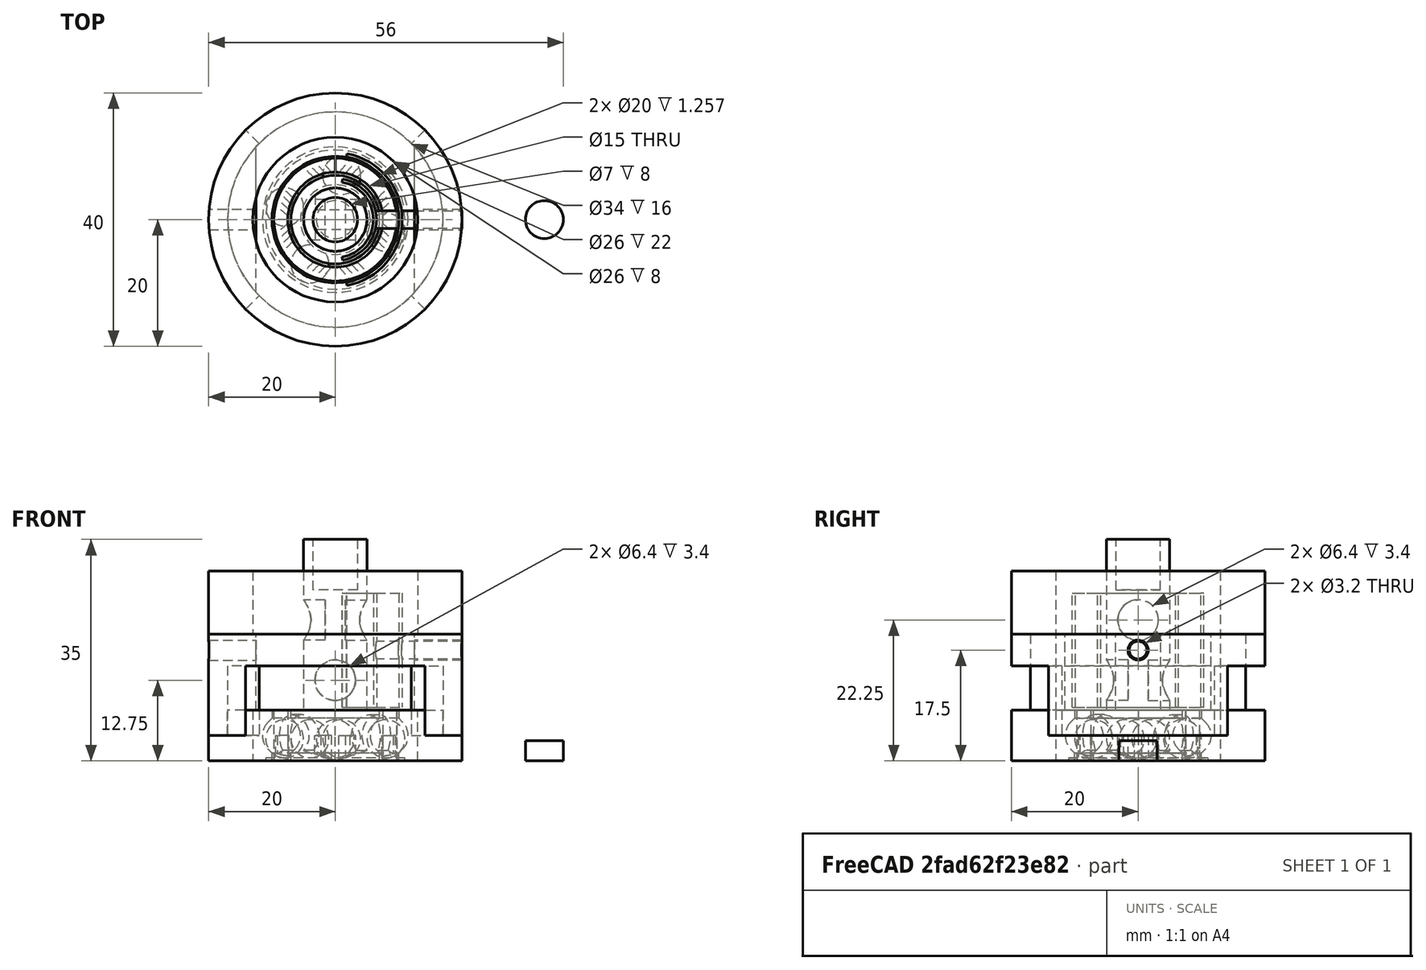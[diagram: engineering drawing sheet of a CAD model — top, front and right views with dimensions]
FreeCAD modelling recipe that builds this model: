
FCSTD DOCUMENT  (FreeCAD 1.2R20260106 (Git shallow))
Label: laser
License: MIT
LicenseURL: https://en.wikipedia.org/wiki/MIT_License
objects: Sketcher::SketchObject×27, App::FeaturePython×20, App::Link×11, PartDesign::Pocket×10, PartDesign::SubShapeBinder×10, PartDesign::Pad×9, App::Point×8, PartDesign::Body×6, Part::Sphere×6, PartDesign::Plane×5, Part::FeaturePython×4, PartDesign::Revolution×2, Part::Cylinder×2, PartDesign::Mirrored×2, Part::Compound×1, Spreadsheet::Sheet×1, Part::Extrusion×1, Part::Loft×1, Assembly::ViewGroup×1, Part::MultiFuse×1, +4 more types
note: 159 computed .brp shape members not serialized (recipe doc carries the construction recipe); baked Part::Feature solids carry a one-line shape summary decoded from their .brp

FEATURE [Sketcher::SketchObject] Sketch
  ArcFitTolerance = 1e-06
  AttachmentSupport = -> [XY_Plane]
  ExternalTypes = [0]
  FullyConstrained = true
  MakeInternals = false
  MapMode = 5
  sketch-geometry (2):
    g0: Circle CenterX=0 CenterY=0 CenterZ=0 NormalX=0 NormalY=0 NormalZ=1 AngleXU=0 Radius=5
    g1: GeomPoint X=0 Y=0 Z=0
  constraints (3):
    c: Diameter(g0) = 10
    c: Coincident(g1,g-1)
    c: Coincident(g0,g1)
FEATURE [PartDesign::Pad] Pad
  Direction = (0,0,1)
  Length = 35
  Length2 = 10
  Profile = -> Sketch
  ReferenceAxis = -> Sketch [N_Axis]
  Refine = true
  SideType = 0
  Suppressed = false
  Type = 0
  Type2 = 0
FEATURE [Sketcher::SketchObject] Sketch019
  ArcFitTolerance = 1e-06
  ExternalTypes = [0]
  FullyConstrained = true
  MakeInternals = false
  MapMode = 5
  Placement = pos=(0,0,35) rot=(0,0,1;0rad)
  sketch-geometry (1):
    g0: Circle CenterX=0 CenterY=0 CenterZ=0 NormalX=0 NormalY=0 NormalZ=1 AngleXU=0 Radius=3.5
  constraints (2):
    c: Diameter(g0) = 7
    c: Coincident(g0,g-1)
FEATURE [PartDesign::Pocket] Pocket007
  BaseFeature = -> Pad
  Direction = (0,0,-1)
  Length = 8
  Length2 = 5
  Profile = -> Sketch019
  ReferenceAxis = -> Sketch019 [N_Axis]
  Refine = true
  SideType = 0
  Suppressed = false
  Type = 0
  Type2 = 0
FEATURE [App::Link] rotor  label="rotor001"
  LinkPlacement = pos=(0,0,0) rot=(0,0,1;2.35834rad)
  LinkedObject = -> Body
  Placement = pos=(0,0,0) rot=(0,0,1;2.35834rad)
FEATURE [Sketcher::SketchObject] Sketch031
  ArcFitTolerance = 1e-06
  AttachmentSupport = -> [Pocket007]
  ExternalGeometry = -> [Pad]
  ExternalTypes = [0]
  FullyConstrained = true
  MakeInternals = false
  MapMode = 5
  Placement = pos=(0,0,35) rot=(0,0,1;0rad)
  sketch-geometry (4):
    g0: LineSegment StartX=0 StartY=0 StartZ=0 EndX=3e-16 EndY=5 EndZ=0
    g1: LineSegment StartX=0 StartY=0 StartZ=0 EndX=-5 EndY=-1e-16 EndZ=0
    g2: LineSegment StartX=0 StartY=0 StartZ=0 EndX=5 EndY=0 EndZ=0
    g3: LineSegment StartX=0 StartY=0 StartZ=0 EndX=-3.305e-13 EndY=-5 EndZ=0
  constraints (12):
    c: Coincident(g0,g-1)
    c: PointOnObject(g0,g-3)
    c: Angle(g-1,g0) = 1.5708
    c: Coincident(g1,g0)
    c: PointOnObject(g1,g-3)
    c: Angle(g1,g-1) = 3.14159
    c: Coincident(g3,g2)
    c: Coincident(g2,g0)
    c: PointOnObject(g3,g-3)
    c: PointOnObject(g2,g-3)
    c: Angle(g-1,g2) = 0
    c: Angle(g3,g-1) = 1.5708
FEATURE [PartDesign::Plane] DatumPlane  label="p2"
  AttachmentOffset = pos=(0,0,0) rot=(0,1,0;3.14159rad)
  AttachmentSupport = -> [Sketch031]
  Length = 60.9545
  MapMode = 7
  Placement = pos=(3e-16,5,35) rot=(0,0.707107,0.707107;3.14159rad)
  ResizeMode = 0
  Width = 70.9545
FEATURE [PartDesign::Plane] DatumPlane003  label="p3"
  AttachmentOffset = pos=(0,0,0) rot=(0,1,0;3.14159rad)
  AttachmentSupport = -> [Sketch031]
  Length = 60.9545
  MapMode = 7
  Placement = pos=(-5,-1e-16,35) rot=(-0.57735,0.57735,0.57735;4.18879rad)
  ResizeMode = 0
  Width = 70.9545
FEATURE [PartDesign::Plane] DatumPlane004  label="p4"
  AttachmentOffset = pos=(0,0,0) rot=(0,1,0;3.14159rad)
  AttachmentSupport = -> [Sketch031]
  Length = 60.9545
  MapMode = 7
  Placement = pos=(5,0,35) rot=(0.57735,0.57735,0.57735;2.0944rad)
  ResizeMode = 0
  Width = 70.9545
FEATURE [PartDesign::Plane] DatumPlane002  label="p1"
  AttachmentOffset = pos=(0,0,0) rot=(0,1,0;3.14159rad)
  AttachmentSupport = -> [Sketch031]
  Length = 60.9545
  MapMode = 7
  Placement = pos=(-3.305e-13,-5,35) rot=(-1,0,0;4.71239rad)
  ResizeMode = 0
  Width = 70.9545
FEATURE [Sketcher::SketchObject] Sketch034
  ArcFitTolerance = 1e-06
  AttachmentSupport = -> [XZ_Plane]
  ExternalTypes = [0]
  FullyConstrained = true
  MakeInternals = false
  MapMode = 5
  Placement = pos=(0,0,0) rot=(1,0,0;1.5708rad)
  expr: Constraints[13] = Spreadsheet.bearing_ball_radius
  expr: Constraints[38] = Spreadsheet.bearing_ball_radius + Spreadsheet.bearing_ball_radius_extra_play / 2
  sketch-geometry (20):
    g0: ArcOfCircle CenterX=8.5 CenterY=4 CenterZ=0 NormalX=0 NormalY=0 NormalZ=1 AngleXU=0 Radius=3 StartAngle=2.35619 EndAngle=3.14159
    g1: LineSegment StartX=6.37868 StartY=6.12132 StartZ=0 EndX=7 EndY=6.74264 EndZ=0
    g2: LineSegment StartX=7 StartY=6.74264 StartZ=0 EndX=7 EndY=8 EndZ=0
    g3: LineSegment StartX=7 StartY=8 StartZ=0 EndX=0 EndY=8 EndZ=0
    g4: LineSegment StartX=0 StartY=0 StartZ=0 EndX=7 EndY=0 EndZ=0
    g5: GeomPoint [constr] X=8.5 Y=4 Z=0
    g6: ArcOfCircle CenterX=8.5 CenterY=4 CenterZ=0 NormalX=0 NormalY=0 NormalZ=1 AngleXU=0 Radius=3 StartAngle=3.14159 EndAngle=3.92699
    g7: LineSegment StartX=6.37868 StartY=1.87868 StartZ=0 EndX=7 EndY=1.25736 EndZ=0
    g8: LineSegment StartX=7 StartY=0 StartZ=0 EndX=7 EndY=1.25736 EndZ=0
    g9: LineSegment [constr] StartX=7 StartY=6.74264 StartZ=0 EndX=10 EndY=6.74264 EndZ=0
    g10: GeomPoint [constr] X=8.5 Y=6.74264 Z=0
    g11: LineSegment [constr] StartX=8.5 StartY=6.74264 StartZ=0 EndX=8.5 EndY=0 EndZ=0
    g12: GeomPoint [constr] X=8.5 Y=4 Z=0
    g13: LineSegment [constr] StartX=8.5 StartY=4 StartZ=0 EndX=5 EndY=4 EndZ=0
    g14: LineSegment [constr] StartX=5 StartY=0 StartZ=0 EndX=5 EndY=8 EndZ=0
    g15: GeomPoint [constr] X=5 Y=4 Z=0
    g16: LineSegment StartX=0 StartY=8 StartZ=0 EndX=0 EndY=0 EndZ=0
    g17: LineSegment [constr] StartX=5.5 StartY=4 StartZ=0 EndX=8.5 EndY=4 EndZ=0
    g18: LineSegment [constr] StartX=7 StartY=6.74264 StartZ=0 EndX=7 EndY=1.25736 EndZ=0
    g19: LineSegment [constr] StartX=5.5 StartY=4 StartZ=0 EndX=5 EndY=4 EndZ=0
  constraints (46):
    c: Angle(g-1,g1) = 0.785398
    c: Tangent(g1,g0) = 1.5708
    c: Vertical(g2)
    c: Coincident(g2,g1)
    c: Horizontal(g3)
    c: Coincident(g3,g2)
    c: PointOnObject(g4,g-1)
    c: Coincident(g0,g5)
    c: Coincident(g6,g0)
    c: Angle(g-1,g7) = -0.785398
    c: Tangent(g7,g6) = -1.5708
    c: Coincident(g8,g4)
    c: Coincident(g7,g8)
    c: Distance(g9) = 3
    c: Horizontal(g9)
    c: Coincident(g9,g1)
    c: Symmetric(g9,g9,g10)
    c: Coincident(g11,g10)
    c: PointOnObject(g11,g-1)
    c: Vertical(g11)
    c: PointOnObject(g12,g11)
    c: Vertical(g8)
    c: Coincident(g0,g12)
    c: Coincident(g13,g0)
    c: Equal(g8,g2)
    c: Horizontal(g13)
    c: PointOnObject(g3,g-2)
    c: Coincident(g4,g-1)
    c: Vertical(g14)
    c: Coincident(g14,g-3)
    c: PointOnObject(g14,g3)
    c: Symmetric(g14,g14,g15)
    c: Coincident(g16,g3)
    c: Coincident(g16,g4)
    c: Coincident(g6,g0)
    c: PointOnObject(g0,g13)
    c: Coincident(g17,g0)
    c: Coincident(g17,g0)
    c: Distance(g17) = 3
    c: Coincident(g18,g1)
    c: Coincident(g18,g7)
    c: Coincident(g19,g0)
    c: Coincident(g19,g15)
    c: Distance(g19) = 0.5
    c: Coincident(g13,g15)
    c: Distance(g16,g16) = 8
FEATURE [PartDesign::Revolution] Revolution
  Angle = 360
  Angle2 = 60
  Axis = (0,2e-16,1)
  Base = (0,0,0)
  BaseFeature = -> Pocket007
  FuseOrder = 1
  Profile = -> Sketch034
  ReferenceAxis = -> Sketch034 [V_Axis]
  Refine = true
  Reversed = true
  Suppressed = false
  Type = 0
FEATURE [Sketcher::SketchObject] Sketch038
  ArcFitTolerance = 1e-06
  AttachmentSupport = -> [Revolution]
  ExternalGeometry = -> [Revolution]
  ExternalTypes = [0]
  FullyConstrained = true
  MakeInternals = false
  MapMode = 5
  Placement = pos=(0,0,35) rot=(0,0,1;0rad)
  sketch-geometry (3):
    g0: Circle CenterX=0 CenterY=0 CenterZ=0 NormalX=0 NormalY=0 NormalZ=1 AngleXU=0 Radius=5
    g1: GeomPoint X=5 Y=0 Z=0
    g2: Circle [constr] CenterX=0 CenterY=0 CenterZ=0 NormalX=0 NormalY=0 NormalZ=1 AngleXU=0 Radius=5
  constraints (6):
    c: Coincident(g0,g-1)
    c: PointOnObject(g1,g0)
    c: PointOnObject(g1,g-1)
    c: Coincident(g2,g0)
    c: PointOnObject(g1,g2)
    c: PointOnObject(g1,g-3)
FEATURE [Sketcher::SketchObject] Sketch041
  ArcFitTolerance = 1e-06
  AttachmentSupport = -> [XY_Plane012]
  ExternalTypes = [0]
  FullyConstrained = true
  MakeInternals = false
  MapMode = 5
  sketch-geometry (2):
    g0: Circle CenterX=0 CenterY=0 CenterZ=0 NormalX=0 NormalY=0 NormalZ=1 AngleXU=0 Radius=13
    g1: Circle CenterX=0 CenterY=0 CenterZ=0 NormalX=0 NormalY=0 NormalZ=1 AngleXU=0 Radius=20
  constraints (4):
    c: Diameter(g0) = 26
    c: Coincident(g0,g-1)
    c: Diameter(g1) = 40
    c: Coincident(g1,g0)
FEATURE [PartDesign::Pad] Pad018
  Direction = (0,0,1)
  Length = 8
  Length2 = 10
  Profile = -> Sketch041
  ReferenceAxis = -> Sketch041 [N_Axis]
  Refine = true
  SideType = 0
  Suppressed = false
  Type = 0
  Type2 = 0
FEATURE [Sketcher::SketchObject] Sketch042
  ArcFitTolerance = 1e-06
  AttachmentSupport = -> [Pad018]
  ExternalGeometry = -> [Pad018]
  ExternalTypes = [0]
  FullyConstrained = true
  MakeInternals = false
  MapMode = 5
  Placement = pos=(0,0,8) rot=(0,0,1;0rad)
  sketch-geometry (10):
    g0: ArcOfCircle CenterX=0 CenterY=0 CenterZ=0 NormalX=0 NormalY=0 NormalZ=1 AngleXU=0 Radius=20 StartAngle=5.49779 EndAngle=7.06858
    g1: ArcOfCircle CenterX=0 CenterY=0 CenterZ=0 NormalX=0 NormalY=0 NormalZ=1 AngleXU=0 Radius=17 StartAngle=5.49779 EndAngle=7.06858
    g2: LineSegment StartX=12.0208 StartY=-12.0208 StartZ=0 EndX=14.1421 EndY=-14.1421 EndZ=0
    g3: LineSegment StartX=12.0208 StartY=12.0208 StartZ=0 EndX=14.1421 EndY=14.1421 EndZ=0
    g4: LineSegment [constr] StartX=0 StartY=0 StartZ=0 EndX=12.0208 EndY=12.0208 EndZ=0
    g5: ArcOfCircle CenterX=0 CenterY=0 CenterZ=0 NormalX=0 NormalY=0 NormalZ=1 AngleXU=0 Radius=20 StartAngle=2.35619 EndAngle=3.92699
    g6: ArcOfCircle CenterX=0 CenterY=0 CenterZ=0 NormalX=0 NormalY=0 NormalZ=1 AngleXU=0 Radius=17 StartAngle=2.35619 EndAngle=3.92699
    g7: LineSegment [constr] StartX=0 StartY=0 StartZ=0 EndX=-12.0208 EndY=-12.0208 EndZ=0
    g8: LineSegment StartX=-12.0208 StartY=12.0208 StartZ=0 EndX=-14.1421 EndY=14.1421 EndZ=0
    g9: LineSegment StartX=-12.0208 StartY=-12.0208 StartZ=0 EndX=-14.1421 EndY=-14.1421 EndZ=0
  constraints (28):
    c: Angle(g0) = 1.5708
    c: Coincident(g0,g-1)
    c: PointOnObject(g0,g-3)
    c: Angle(g1) = 1.5708
    c: Coincident(g1,g0)
    c: Coincident(g2,g1)
    c: Coincident(g2,g0)
    c: Coincident(g3,g1)
    c: Coincident(g3,g0)
    c: Distance(g3) = 3
    c: Coincident(g4,g0)
    c: Coincident(g4,g1)
    c: Parallel(g3,g4)
    c: Angle(g-1,g4) = 0.785398
    c: Angle(g5) = 1.5708
    c: Coincident(g5,g0)
    c: PointOnObject(g5,g-3)
    c: Angle(g6) = 1.5708
    c: Coincident(g6,g0)
    c: Coincident(g7,g0)
    c: Coincident(g7,g6)
    c: Angle(g7,g-1) = 2.35619
    c: Coincident(g8,g6)
    c: Coincident(g8,g5)
    c: Coincident(g9,g6)
    c: Coincident(g9,g5)
    c: Distance(g8) = 3
    c: Parallel(g9,g7)
FEATURE [PartDesign::Pocket] Pocket018
  BaseFeature = -> Pad018
  Direction = (0,0,-1)
  Length = 4
  Length2 = 5
  Profile = -> Sketch042
  ReferenceAxis = -> Sketch042 [N_Axis]
  Refine = true
  SideType = 0
  Suppressed = false
  Type = 0
  Type2 = 0
FEATURE [PartDesign::Body] Body011  label="bearing_holder"
  AllowCompound = false
  Group = -> [Sketch041,Pad018,Sketch042,Pocket018]
  Origin = -> Origin012
  Tip = -> Pocket018
FEATURE [PartDesign::SubShapeBinder] Binder009
  BindCopyOnChange = 0
  BindMode = 0
  ClaimChildren = false
  Context = -> Body012 [Binder009.]
  Fuse = false
  MakeFace = true
  OffsetFill = false
  OffsetIntersection = false
  OffsetJoinType = 0
  OffsetOpenResult = false
  PartialLoad = false
  Refine = true
  Relative = true
  Support = -> [Body011]
  _Version = 2
FEATURE [Sketcher::SketchObject] Sketch044
  ArcFitTolerance = 1e-06
  AttachmentOffset = pos=(0,0,15) rot=(0,0,1;0rad)
  AttachmentSupport = -> [Binder009]
  ExternalTypes = [0]
  FullyConstrained = true
  MakeInternals = false
  MapMode = 5
  Placement = pos=(0,0,15) rot=(0,0,1;3.14159rad)
  sketch-geometry (15):
    g0: Circle CenterX=0 CenterY=0 CenterZ=0 NormalX=0 NormalY=0 NormalZ=1 AngleXU=0 Radius=20
    g1: Circle [constr] CenterX=0 CenterY=0 CenterZ=0 NormalX=0 NormalY=0 NormalZ=1 AngleXU=0 Radius=6.5
    g2: GeomPoint [constr] X=5 Y=0 Z=0
    g3: LineSegment [constr] StartX=6.5 StartY=0 StartZ=0 EndX=5 EndY=0 EndZ=0
    g4: LineSegment StartX=12.5 StartY=11.5217 StartZ=0 EndX=12.5 EndY=-11.5217 EndZ=0
    g5: ArcOfCircle CenterX=-1.6699e-12 CenterY=-6e-16 CenterZ=0 NormalX=0 NormalY=0 NormalZ=1 AngleXU=0 Radius=17 StartAngle=0.744696 EndAngle=2.3969
    g6: GeomPoint X=12.5 Y=0 Z=0
    g7: LineSegment StartX=-12.5 StartY=11.5217 StartZ=0 EndX=-12.5 EndY=-11.5217 EndZ=0
    g8: ArcOfCircle CenterX=0 CenterY=0 CenterZ=0 NormalX=0 NormalY=0 NormalZ=1 AngleXU=0 Radius=17 StartAngle=3.88629 EndAngle=5.53849
    g9: GeomPoint X=-12.5 Y=0 Z=0
    g10: GeomPoint X=-6.5 Y=0 Z=0
    g11: LineSegment [constr] StartX=-12.5 StartY=0 StartZ=0 EndX=-6.5 EndY=0 EndZ=0
    g12: LineSegment [constr] StartX=12.5 StartY=0 StartZ=0 EndX=6.5 EndY=0 EndZ=0
    g13: Circle [constr] CenterX=-1.6699e-12 CenterY=-6e-16 CenterZ=0 NormalX=0 NormalY=0 NormalZ=1 AngleXU=0 Radius=17
    g14: GeomPoint [constr] X=-12.0208 Y=-12.0208 Z=0
  constraints (35):
    c: Coincident(g0,g-1)
    c: Coincident(g1,g0)
    c: PointOnObject(g2,g-5)
    c: PointOnObject(g3,g1)
    c: Coincident(g3,g2)
    c: PointOnObject(g2,g-1)
    c: PointOnObject(g3,g-1)
    c: Distance(g3,g3) = 1.5
    c: PointOnObject(g4,g5)
    c: PointOnObject(g-3,g0)
    c: Coincident(g8,g4)
    c: PointOnObject(g5,g4)
    c: Symmetric(g4,g4,g6)
    c: PointOnObject(g6,g-1)
    c: PointOnObject(g9,g7)
    c: PointOnObject(g10,g1)
    c: PointOnObject(g10,g-1)
    c: PointOnObject(g9,g-1)
    c: Coincident(g11,g9)
    c: Coincident(g11,g10)
    c: Coincident(g12,g6)
    c: Coincident(g12,g3)
    c: Equal(g11,g12)
    c: Coincident(g7,g5)
    c: Coincident(g7,g8)
    c: Vertical(g7)
    c: Distance(g12,g12) = 6
    c: Vertical(g4)
    c: Equal(g4,g7)
    c: Coincident(g8,g0)
    c: Coincident(g13,g5)
    c: PointOnObject(g-4,g13)
    c: PointOnObject(g5,g13)
    c: PointOnObject(g14,g13)
    c: Coincident(g14,g-4)
FEATURE [PartDesign::Pad] Pad021
  Direction = (0,0,1)
  Length = 5
  Length2 = 10
  Profile = -> Sketch044
  ReferenceAxis = -> Sketch044 [N_Axis]
  Refine = true
  SideType = 0
  Suppressed = false
  Type = 0
  Type2 = 0
FEATURE [Sketcher::SketchObject] Sketch045
  ArcFitTolerance = 1e-06
  AttachmentSupport = -> [Pad021]
  ExternalGeometry = -> [Binder009]
  ExternalTypes = [0]
  FullyConstrained = true
  MakeInternals = false
  MapMode = 5
  Placement = pos=(0,0,15) rot=(1,0,0;3.14159rad)
  sketch-geometry (12):
    g0: ArcOfCircle CenterX=0 CenterY=0 CenterZ=0 NormalX=0 NormalY=0 NormalZ=1 AngleXU=0 Radius=20 StartAngle=2.35619 EndAngle=3.92699
    g1: ArcOfCircle CenterX=0 CenterY=0 CenterZ=0 NormalX=0 NormalY=0 NormalZ=1 AngleXU=0 Radius=17 StartAngle=2.35619 EndAngle=3.92699
    g2: ArcOfCircle CenterX=0 CenterY=0 CenterZ=0 NormalX=0 NormalY=0 NormalZ=1 AngleXU=0 Radius=20 StartAngle=5.49779 EndAngle=7.06858
    g3: ArcOfCircle CenterX=0 CenterY=0 CenterZ=0 NormalX=0 NormalY=0 NormalZ=1 AngleXU=0 Radius=17 StartAngle=5.49779 EndAngle=7.06858
    g4: LineSegment StartX=-14.1421 StartY=-14.1421 StartZ=0 EndX=-12.0208 EndY=-12.0208 EndZ=0
    g5: LineSegment StartX=-14.1421 StartY=14.1421 StartZ=0 EndX=-12.0208 EndY=12.0208 EndZ=0
    g6: LineSegment StartX=14.1421 StartY=-14.1421 StartZ=0 EndX=12.0208 EndY=-12.0208 EndZ=0
    g7: LineSegment StartX=14.1421 StartY=14.1421 StartZ=0 EndX=12.0208 EndY=12.0208 EndZ=0
    g8: LineSegment [constr] StartX=0 StartY=0 StartZ=0 EndX=12.0208 EndY=-12.0208 EndZ=0
    g9: LineSegment [constr] StartX=-12.0208 StartY=-12.0208 StartZ=0 EndX=0 EndY=0 EndZ=0
    g10: LineSegment [constr] StartX=12.0208 StartY=-12.0208 StartZ=0 EndX=14.1421 EndY=-14.1421 EndZ=0
    g11: LineSegment [constr] StartX=-14.1421 StartY=-14.1421 StartZ=0 EndX=-12.0208 EndY=-12.0208 EndZ=0
  constraints (28):
    c: Coincident(g0,g-1)
    c: Coincident(g0,g-4)
    c: Coincident(g1,g0)
    c: Coincident(g1,g-3)
    c: Coincident(g2,g0)
    c: Coincident(g2,g-7)
    c: Coincident(g3,g0)
    c: Coincident(g3,g-5)
    c: Coincident(g4,g0)
    c: Coincident(g4,g1)
    c: Coincident(g5,g0)
    c: Coincident(g5,g1)
    c: Coincident(g6,g2)
    c: Coincident(g6,g3)
    c: Coincident(g7,g2)
    c: Coincident(g7,g3)
    c: Coincident(g8,g0)
    c: Coincident(g8,g3)
    c: Coincident(g9,g1)
    c: Coincident(g9,g0)
    c: Parallel(g4,g9)
    c: Parallel(g8,g6)
    c: Coincident(g10,g-5)
    c: Coincident(g10,g-6)
    c: Parallel(g6,g10)
    c: Coincident(g11,g-4)
    c: Coincident(g11,g-3)
    c: Parallel(g4,g11)
FEATURE [PartDesign::Pad] Pad022
  BaseFeature = -> Pad021
  Direction = (0,0,-1)
  Length = 10
  Length2 = 10
  Profile = -> Sketch045
  ReferenceAxis = -> Sketch045 [N_Axis]
  Refine = true
  SideType = 0
  Suppressed = false
  Type = 3
  Type2 = 0
  UpToFace = -> Binder009 [Face7]
FEATURE [Part::Cylinder] Cylinder001  label="magnet"
  Angle = 360
  AttacherType = Attacher::AttachEngine3D
  FirstAngle = 0
  Height = 3.2
  Placement = pos=(33,0,0) rot=(0,0,1;0rad)
  Radius = 3
  SecondAngle = 0
FEATURE [PartDesign::SubShapeBinder] Binder010
  BindCopyOnChange = 0
  BindMode = 0
  ClaimChildren = false
  Context = -> Body012 [Binder010.]
  Fuse = false
  MakeFace = true
  OffsetFill = false
  OffsetIntersection = false
  OffsetJoinType = 0
  OffsetOpenResult = false
  PartialLoad = false
  Refine = true
  Relative = true
  Support = -> [Body]
  _Version = 2
FEATURE [Sketcher::SketchObject] Sketch046
  ArcFitTolerance = 1e-06
  AttachmentOffset = pos=(0,0,8.5) rot=(0,0,1;0rad)
  AttachmentSupport = -> [XY_Plane014]
  ExternalTypes = [0]
  FullyConstrained = true
  MakeInternals = false
  MapMode = 5
  Placement = pos=(0,0,8.5) rot=(0,0,1;0rad)
  sketch-geometry (11):
    g0: GeomPoint X=5 Y=0 Z=0
    g1: GeomPoint X=6 Y=0 Z=0
    g2: LineSegment [constr] StartX=5 StartY=0 StartZ=0 EndX=6 EndY=0 EndZ=0
    g3: LineSegment [constr] StartX=1.04189 StartY=5.90885 StartZ=0 EndX=1.12871 EndY=6.40125 EndZ=0
    g4: ArcOfCircle CenterX=0 CenterY=0 CenterZ=0 NormalX=0 NormalY=0 NormalZ=1 AngleXU=0 Radius=6 StartAngle=4.88692 EndAngle=7.67945
    g5: LineSegment [constr] StartX=1.04189 StartY=-5.90885 StartZ=0 EndX=0 EndY=0 EndZ=0
    g6: LineSegment [constr] StartX=0 StartY=0 StartZ=0 EndX=1.04189 EndY=5.90885 EndZ=0
    g7: ArcOfCircle CenterX=0 CenterY=0 CenterZ=0 NormalX=0 NormalY=0 NormalZ=1 AngleXU=0 Radius=6.5 StartAngle=4.88692 EndAngle=7.67945
    g8: LineSegment [constr] StartX=1.12871 StartY=-6.40125 StartZ=0 EndX=1.04189 EndY=-5.90885 EndZ=0
    g9: LineSegment StartX=1.12871 StartY=-6.40125 StartZ=0 EndX=1.04189 EndY=-5.90885 EndZ=0
    g10: LineSegment StartX=1.12871 StartY=6.40125 StartZ=0 EndX=1.04189 EndY=5.90885 EndZ=0
  constraints (26):
    c: PointOnObject(g0,g-3)
    c: PointOnObject(g1,g4)
    c: PointOnObject(g0,g-1)
    c: PointOnObject(g1,g-1)
    c: Coincident(g2,g0)
    c: Coincident(g2,g1)
    c: Distance(g2,g2) = 1
    c: Coincident(g5,g-1)
    c: Angle(g-1,g6) = 1.39626
    c: Angle(g5,g-1) = 1.39626
    c: Coincident(g6,g4)
    c: Coincident(g4,g5)
    c: Coincident(g7,g4)
    c: Parallel(g3,g6)
    c: Coincident(g3,g7)
    c: Coincident(g6,g4)
    c: Coincident(g3,g4)
    c: Distance(g3,g3) = 0.5
    c: Coincident(g8,g7)
    c: Coincident(g8,g4)
    c: Parallel(g8,g5)
    c: Coincident(g4,g5)
    c: Coincident(g9,g7)
    c: Coincident(g9,g4)
    c: Coincident(g10,g3)
    c: Coincident(g10,g3)
FEATURE [PartDesign::SubShapeBinder] Binder011
  BindCopyOnChange = 0
  BindMode = 0
  ClaimChildren = false
  Context = -> Body013 [Binder011.]
  Fuse = false
  MakeFace = true
  OffsetFill = false
  OffsetIntersection = false
  OffsetJoinType = 0
  OffsetOpenResult = false
  PartialLoad = false
  Refine = true
  Relative = true
  Support = -> [Body]
  _Version = 2
FEATURE [PartDesign::Pad] Pad023
  Direction = (0,0,1)
  Length = 18
  Length2 = 10
  Profile = -> Sketch046
  ReferenceAxis = -> Sketch046 [N_Axis]
  Refine = true
  SideType = 0
  Suppressed = false
  Type = 0
  Type2 = 0
FEATURE [Sketcher::SketchObject] Sketch047
  ArcFitTolerance = 1e-06
  AttachmentSupport = -> [Pad023]
  ExternalGeometry = -> [Pad023]
  ExternalTypes = [0]
  FullyConstrained = true
  MakeInternals = false
  MapMode = 5
  Placement = pos=(0,0,26.5) rot=(0,0,1;0rad)
  sketch-geometry (3):
    g0: GeomPoint X=6.5 Y=0 Z=0
    g1: GeomPoint X=6 Y=0 Z=0
    g2: LineSegment StartX=6 StartY=0 StartZ=0 EndX=6.5 EndY=0 EndZ=0
  constraints (6):
    c: PointOnObject(g0,g-4)
    c: PointOnObject(g1,g-3)
    c: Coincident(g2,g1)
    c: Coincident(g2,g0)
    c: Horizontal(g2)
    c: PointOnObject(g0,g-1)
FEATURE [PartDesign::Plane] DatumPlane006
  AttachmentOffset = pos=(0,0,0) rot=(0,1,0;3.14159rad)
  AttachmentSupport = -> [Sketch047]
  Length = 60.1489
  MapMode = 7
  Placement = pos=(6.5,0,26.5) rot=(0.57735,0.57735,0.57735;2.0944rad)
  ResizeMode = 0
  Width = 61.6489
FEATURE [Sketcher::SketchObject] Sketch049
  ArcFitTolerance = 1e-06
  AttachmentOffset = pos=(0,0,-0.5) rot=(0,0,1;0rad)
  AttachmentSupport = -> [DatumPlane006]
  ExternalGeometry = -> [Pad023]
  ExternalTypes = [0]
  FullyConstrained = true
  MakeInternals = false
  MapMode = 5
  Placement = pos=(6,0,26.5) rot=(0.57735,0.57735,0.57735;2.0944rad)
  sketch-geometry (4):
    g0: LineSegment [constr] StartX=-6.40125 StartY=0 StartZ=0 EndX=6.40125 EndY=-18 EndZ=0
    g1: LineSegment [constr] StartX=-6.40125 StartY=-18 StartZ=0 EndX=6.40125 EndY=0 EndZ=0
    g2: GeomPoint [constr] X=0 Y=-9 Z=0
    g3: Circle CenterX=0 CenterY=-9 CenterZ=0 NormalX=0 NormalY=0 NormalZ=1 AngleXU=0 Radius=1.4
  constraints (7):
    c: Coincident(g0,g-5)
    c: Coincident(g0,g-6)
    c: Coincident(g1,g-6)
    c: Coincident(g1,g-5)
    c: Symmetric(g0,g0,g2)
    c: Diameter(g3) = 2.8
    c: Coincident(g3,g2)
FEATURE [PartDesign::Pad] Pad024
  BaseFeature = -> Pad023
  Direction = (1,0,0)
  Length = 14
  Length2 = 10
  Profile = -> Sketch049
  ReferenceAxis = -> Sketch049 [N_Axis]
  Refine = true
  SideType = 0
  Suppressed = false
  Type = 0
  Type2 = 0
FEATURE [Sketcher::SketchObject] Sketch050
  ArcFitTolerance = 1e-06
  AttachmentOffset = pos=(0,0,8.5) rot=(0,0,1;0rad)
  AttachmentSupport = -> [XY_Plane014]
  ExternalGeometry = -> [Pad023]
  ExternalTypes = [0]
  FullyConstrained = true
  MakeInternals = false
  MapMode = 5
  Placement = pos=(0,0,8.5) rot=(0,0,1;0rad)
  sketch-geometry (7):
    g0: ArcOfCircle CenterX=0 CenterY=0 CenterZ=0 NormalX=0 NormalY=0 NormalZ=1 AngleXU=0 Radius=10.054 StartAngle=4.88692 EndAngle=7.67945
    g1: LineSegment [constr] StartX=1.83268 StartY=-10.3937 StartZ=0 EndX=1.74586 EndY=-9.90125 EndZ=0
    g2: LineSegment StartX=1.83268 StartY=10.3937 StartZ=0 EndX=1.74586 EndY=9.90125 EndZ=0
    g3: LineSegment StartX=1.83268 StartY=-10.3937 StartZ=0 EndX=1.74586 EndY=-9.90125 EndZ=0
    g4: ArcOfCircle CenterX=0 CenterY=0 CenterZ=0 NormalX=0 NormalY=0 NormalZ=1 AngleXU=0 Radius=10.554 StartAngle=4.88692 EndAngle=7.67945
    g5: LineSegment [constr] StartX=1.74586 StartY=-9.90125 StartZ=0 EndX=1.12871 EndY=-6.40125 EndZ=0
    g6: LineSegment [constr] StartX=1.12871 StartY=6.40125 StartZ=0 EndX=1.74586 EndY=9.90125 EndZ=0
  constraints (18):
    c: Coincident(g1,g0)
    c: Coincident(g2,g0)
    c: Coincident(g3,g0)
    c: Coincident(g0,g-1)
    c: Coincident(g4,g0)
    c: Coincident(g4,g3)
    c: Coincident(g4,g2)
    c: Coincident(g1,g3)
    c: Parallel(g2,g-5)
    c: Parallel(g3,g-6)
    c: Coincident(g5,g0)
    c: Coincident(g5,g-6)
    c: Parallel(g-6,g5)
    c: Coincident(g6,g-5)
    c: Coincident(g6,g0)
    c: Parallel(g6,g-5)
    c: Distance(g2,g2) = 0.5
    c: DistanceY(g6,g6) = 3.5
FEATURE [PartDesign::Pad] Pad025
  BaseFeature = -> Pad024
  Direction = (0,0,1)
  Length = 18
  Length2 = 10
  Profile = -> Sketch050
  ReferenceAxis = -> Sketch050 [N_Axis]
  Refine = true
  SideType = 0
  Suppressed = false
  Type = 0
  Type2 = 0
FEATURE [PartDesign::Body] Body013  label="coil"
  AllowCompound = false
  Group = -> [Sketch046,Binder011,Pad023,Sketch047,DatumPlane006,Sketch049,Pad024,Sketch050,Pad025]
  Origin = -> Origin014
  Tip = -> Pad025
FEATURE [PartDesign::SubShapeBinder] Binder012
  BindCopyOnChange = 0
  BindMode = 0
  ClaimChildren = false
  Context = -> Body012 [Binder012.]
  Fuse = false
  MakeFace = true
  OffsetFill = false
  OffsetIntersection = false
  OffsetJoinType = 0
  OffsetOpenResult = false
  PartialLoad = false
  Refine = true
  Relative = true
  Support = -> [Body013]
  _Version = 2
FEATURE [Sketcher::SketchObject] Sketch051
  ArcFitTolerance = 1e-06
  AttachmentSupport = -> [Pad021]
  ExternalGeometry = -> [Binder012]
  ExternalTypes = [0]
  FullyConstrained = true
  MakeInternals = false
  MapMode = 5
  Placement = pos=(-12.5,0,0) rot=(0.57735,0.57735,0.57735;2.0944rad)
  sketch-geometry (3):
    g0: Circle CenterX=-5e-16 CenterY=17.5 CenterZ=0 NormalX=0 NormalY=0 NormalZ=1 AngleXU=0 Radius=1.6
    g1: GeomPoint [constr] X=0 Y=19.1 Z=0
    g2: GeomPoint [constr] X=0 Y=18.9 Z=0
  constraints (6):
    c: Coincident(g0,g-3)
    c: PointOnObject(g1,g0)
    c: PointOnObject(g2,g-3)
    c: PointOnObject(g2,g-2)
    c: PointOnObject(g1,g-2)
    c: Distance(g1,g2) = 0.2
FEATURE [PartDesign::Pocket] Pocket019
  BaseFeature = -> Pad022
  Direction = (-1,0,0)
  Length = 5
  Length2 = 5
  Profile = -> Sketch051
  ReferenceAxis = -> Sketch051 [N_Axis]
  Refine = true
  SideType = 0
  Suppressed = false
  Type = 1
  Type2 = 0
FEATURE [PartDesign::SubShapeBinder] Binder013
  BindCopyOnChange = 0
  BindMode = 0
  ClaimChildren = false
  Context = -> Body012 [Binder013.]
  Fuse = false
  MakeFace = true
  OffsetFill = false
  OffsetIntersection = false
  OffsetJoinType = 0
  OffsetOpenResult = false
  PartialLoad = false
  Placement = pos=(0,0,0) rot=(0,0,1;3.14159rad)
  Refine = true
  Relative = true
  Support = -> [Body013]
  _Version = 2
FEATURE [Sketcher::SketchObject] Sketch052
  ArcFitTolerance = 1e-06
  AttachmentSupport = -> [Pocket019]
  ExternalGeometry = -> [Binder013]
  ExternalTypes = [0]
  FullyConstrained = true
  MakeInternals = false
  MapMode = 5
  Placement = pos=(12.5,0,0) rot=(0.57735,-0.57735,-0.57735;2.0944rad)
  sketch-geometry (3):
    g0: Circle CenterX=3.4e-15 CenterY=17.5 CenterZ=0 NormalX=0 NormalY=0 NormalZ=1 AngleXU=0 Radius=1.6
    g1: GeomPoint X=0 Y=18.9 Z=0
    g2: GeomPoint [constr] X=0 Y=19.1 Z=0
  constraints (6):
    c: Coincident(g0,g-3)
    c: PointOnObject(g1,g-3)
    c: PointOnObject(g1,g-2)
    c: PointOnObject(g2,g0)
    c: PointOnObject(g2,g-2)
    c: Distance(g2,g1) = 0.2
FEATURE [PartDesign::Pocket] Pocket020
  BaseFeature = -> Pocket019
  Direction = (1,0,0)
  Length = 5
  Length2 = 5
  Profile = -> Sketch052
  ReferenceAxis = -> Sketch052 [N_Axis]
  Refine = true
  SideType = 0
  Suppressed = false
  Type = 1
  Type2 = 0
FEATURE [PartDesign::Body] Body012  label="coil_frame"
  AllowCompound = false
  Group = -> [Binder009,Binder010,Pad021,Sketch044,Sketch045,Pad022,Binder012,Sketch051,Pocket019,Binder013,Sketch052,Pocket020]
  Origin = -> Origin013
  Tip = -> Pocket020
FEATURE [Sketcher::SketchObject] Sketch053
  ArcFitTolerance = 1e-06
  AttachmentSupport = -> [Revolution]
  ExternalGeometry = -> [Revolution]
  ExternalTypes = [0]
  FullyConstrained = true
  MakeInternals = false
  MapMode = 5
  Placement = pos=(0,0,35) rot=(0,0,1;0rad)
  sketch-geometry (4):
    g0: Circle CenterX=0 CenterY=0 CenterZ=0 NormalX=0 NormalY=0 NormalZ=1 AngleXU=0 Radius=5
    g1: Circle CenterX=0 CenterY=0 CenterZ=0 NormalX=0 NormalY=0 NormalZ=1 AngleXU=0 Radius=8.5
    g2: GeomPoint X=5 Y=0 Z=0
    g3: GeomPoint X=5 Y=0 Z=0
  constraints (7):
    c: Coincident(g0,g-1)
    c: Diameter(g1) = 17
    c: Coincident(g1,g0)
    c: PointOnObject(g2,g-3)
    c: PointOnObject(g3,g0)
    c: PointOnObject(g3,g-1)
    c: Coincident(g3,g2)
FEATURE [PartDesign::SubShapeBinder] Binder
  BindCopyOnChange = 0
  BindMode = 0
  ClaimChildren = false
  Context = -> Body007 [Binder.]
  Fuse = false
  MakeFace = true
  OffsetFill = false
  OffsetIntersection = false
  OffsetJoinType = 0
  OffsetOpenResult = false
  PartialLoad = false
  Refine = true
  Relative = true
  Support = -> [Body[Revolution.]]
  _Version = 2
FEATURE [Sketcher::SketchObject] Sketch035
  ArcFitTolerance = 1e-06
  AttachmentSupport = -> [XZ_Plane008]
  ExternalGeometry = -> [Binder]
  ExternalTypes = [0]
  FullyConstrained = true
  MakeInternals = false
  MapMode = 5
  Placement = pos=(0,0,0) rot=(1,0,0;1.5708rad)
  expr: Constraints[25] = Spreadsheet.bearing_ball_radius
  expr: Constraints[6] = Spreadsheet.bearing_ball_radius + Spreadsheet.bearing_ball_radius_extra_play / 2
  sketch-geometry (17):
    g0: LineSegment [constr] StartX=8.5 StartY=8 StartZ=0 EndX=8.5 EndY=0 EndZ=0
    g1: LineSegment StartX=10 StartY=8 StartZ=0 EndX=10 EndY=6.74264 EndZ=0
    g2: LineSegment [constr] StartX=7 StartY=6.74264 StartZ=0 EndX=10 EndY=6.74264 EndZ=0
    g3: GeomPoint [constr] X=8.5 Y=4 Z=0
    g4: ArcOfCircle CenterX=8.5 CenterY=4 CenterZ=0 NormalX=0 NormalY=0 NormalZ=1 AngleXU=0 Radius=3 StartAngle=0 EndAngle=0.785398
    g5: LineSegment StartX=10.6213 StartY=6.12132 StartZ=0 EndX=10 EndY=6.74264 EndZ=0
    g6: ArcOfCircle CenterX=8.5 CenterY=4 CenterZ=0 NormalX=0 NormalY=0 NormalZ=1 AngleXU=0 Radius=3 StartAngle=5.49779 EndAngle=6.28319
    g7: LineSegment StartX=10 StartY=0 StartZ=0 EndX=10 EndY=1.25736 EndZ=0
    g8: LineSegment StartX=10.6213 StartY=1.87868 StartZ=0 EndX=10 EndY=1.25736 EndZ=0
    g9: LineSegment [constr] StartX=8.5 StartY=4 StartZ=0 EndX=11.5 EndY=4 EndZ=0
    g10: LineSegment StartX=10 StartY=8 StartZ=0 EndX=13 EndY=8 EndZ=0
    g11: LineSegment [constr] StartX=7 StartY=8 StartZ=0 EndX=10 EndY=8 EndZ=0
    g12: LineSegment [constr] StartX=7 StartY=1.25736 StartZ=0 EndX=10 EndY=1.25736 EndZ=0
    g13: LineSegment StartX=13 StartY=8 StartZ=0 EndX=13 EndY=0 EndZ=0
    g14: LineSegment StartX=13 StartY=0 StartZ=0 EndX=10 EndY=0 EndZ=0
    g15: LineSegment [constr] StartX=0 StartY=0 StartZ=0 EndX=13 EndY=0 EndZ=0
    g16: LineSegment [constr] StartX=10 StartY=6.74264 StartZ=0 EndX=10 EndY=1.25736 EndZ=0
  constraints (43):
    c: Vertical(g0)
    c: Vertical(g1)
    c: Coincident(g2,g1)
    c: Horizontal(g2)
    c: Symmetric(g0,g0,g3)
    c: PointOnObject(g0,g-1)
    c: Radius(g4) = 3
    c: Angle(g4) = 0.785398
    c: Coincident(g4,g3)
    c: Coincident(g5,g1)
    c: Angle(g6) = 0.785398
    c: Coincident(g6,g3)
    c: Coincident(g6,g4)
    c: PointOnObject(g7,g-1)
    c: Coincident(g8,g7)
    c: Vertical(g7)
    c: Coincident(g9,g3)
    c: Coincident(g9,g4)
    c: Horizontal(g9)
    c: Horizontal(g10)
    c: Tangent(g5,g4) = -1.5708
    c: Tangent(g8,g6) = 1.5708
    c: Coincident(g1,g10)
    c: Coincident(g11,g1)
    c: Horizontal(g11)
    c: Distance(g11) = 3
    c: Coincident(g12,g7)
    c: Horizontal(g12)
    c: Equal(g12,g11)
    c: Coincident(g13,g10)
    c: PointOnObject(g13,g-1)
    c: Vertical(g13)
    c: Coincident(g14,g13)
    c: Coincident(g14,g7)
    c: Coincident(g15,g-1)
    c: Coincident(g15,g13)
    c: DistanceX(g15,g15) = 13
    c: Coincident(g16,g1)
    c: Coincident(g16,g7)
    c: Vertical(g16)
    c: PointOnObject(g0,g11)
    c: Coincident(g11,g-4)
    c: Coincident(g2,g-5)
FEATURE [PartDesign::Revolution] Revolution001
  Angle = 360
  Angle2 = 60
  Axis = (0,2e-16,1)
  Base = (0,0,0)
  FuseOrder = 1
  Placement = pos=(0,0,0) rot=(1,0,0;1.5708rad)
  Profile = -> Sketch035
  ReferenceAxis = -> Sketch035 [V_Axis]
  Refine = true
  Reversed = true
  Suppressed = false
  Type = 0
FEATURE [PartDesign::Body] Body007  label="bearing_body"
  AllowCompound = false
  Group = -> [Sketch035,Revolution001,Binder]
  Origin = -> Origin008
  Tip = -> Revolution001
FEATURE [Part::Cylinder] Cylinder003
  Angle = 360
  AttacherType = Attacher::AttachEngine3D
  FirstAngle = 0
  Height = 0.5
  Radius = 11
  SecondAngle = 0
FEATURE [Part::Sphere] Sphere005
  Angle1 = -90
  Angle2 = 90
  Angle3 = 360
  AttacherType = Attacher::AttachEngine3D
  AttachmentOffset = pos=(8,-2,3) rot=(0,0,1;0rad)
  AttachmentSupport = -> [Cylinder003]
  MapMode = 5
  Placement = pos=(8,-2,3.5) rot=(0,0,1;0rad)
  Radius = 3
  expr: .AttachmentOffset.Base.z = Spreadsheet.bearing_ball_radius
  expr: .Placement.Base.z = Spreadsheet.bearing_ball_radius
  expr: Radius = Spreadsheet.bearing_ball_radius
FEATURE [Part::Sphere] Sphere006
  Angle1 = -90
  Angle2 = 90
  Angle3 = 360
  AttacherType = Attacher::AttachEngine3D
  AttachmentOffset = pos=(1,7,3) rot=(0,0,1;0rad)
  AttachmentSupport = -> [Cylinder003]
  MapMode = 5
  Placement = pos=(1,7,3.5) rot=(0,0,1;0rad)
  Radius = 3
  expr: .AttachmentOffset.Base.z = Spreadsheet.bearing_ball_radius
  expr: .Placement.Base.z = Spreadsheet.bearing_ball_radius
  expr: Radius = Spreadsheet.bearing_ball_radius
FEATURE [Part::Sphere] Sphere007
  Angle1 = -90
  Angle2 = 90
  Angle3 = 360
  AttacherType = Attacher::AttachEngine3D
  AttachmentOffset = pos=(-8,2,3) rot=(0,0,1;0rad)
  AttachmentSupport = -> [Cylinder003]
  MapMode = 5
  Placement = pos=(-8,2,3.5) rot=(0,0,1;0rad)
  Radius = 3
  expr: .AttachmentOffset.Base.z = Spreadsheet.bearing_ball_radius
  expr: .Placement.Base.z = Spreadsheet.bearing_ball_radius
  expr: Radius = Spreadsheet.bearing_ball_radius
FEATURE [Part::Sphere] Sphere008
  Angle1 = -90
  Angle2 = 90
  Angle3 = 360
  AttacherType = Attacher::AttachEngine3D
  AttachmentOffset = pos=(-4,-7,3) rot=(0,0,1;0rad)
  AttachmentSupport = -> [Cylinder003]
  MapMode = 5
  Placement = pos=(-4,-7,3.5) rot=(0,0,1;0rad)
  Radius = 3
  expr: .AttachmentOffset.Base.z = Spreadsheet.bearing_ball_radius
  expr: .Placement.Base.z = Spreadsheet.bearing_ball_radius
  expr: Radius = Spreadsheet.bearing_ball_radius
FEATURE [Part::Sphere] Sphere009
  Angle1 = -90
  Angle2 = 90
  Angle3 = 360
  AttacherType = Attacher::AttachEngine3D
  AttachmentOffset = pos=(0,0,3) rot=(0,0,1;0rad)
  AttachmentSupport = -> [Cylinder003]
  MapMode = 5
  Placement = pos=(0,0,3.5) rot=(0,0,1;0rad)
  Radius = 3
  expr: .AttachmentOffset.Base.z = Spreadsheet.bearing_ball_radius
  expr: .Placement.Base.z = 3.5 mm
  expr: Radius = Spreadsheet.bearing_ball_radius
FEATURE [Part::Compound] Compound002  label="balls"
  Links = -> [Sphere009,Sphere005,Cylinder003,Sphere006,Sphere007,Sphere008]
FEATURE [App::Link] bearing_body  label="bearing_body001"
  LinkedObject = -> Body007
FEATURE [App::FeaturePython] GroundedJoint  # Assembly grounded joint (typed FeaturePython)
  ObjectToGround = -> bearing_body
FEATURE [App::Link] bearing_holder  label="bearing_holder001"
  LinkPlacement = pos=(7.1e-15,3.2e-15,0) rot=(0,0,1;0rad)
  LinkedObject = -> Body011
  Placement = pos=(7.1e-15,3.2e-15,0) rot=(0,0,1;0rad)
FEATURE [App::FeaturePython] Joint  label="Fixed"  # Assembly joint (typed FeaturePython)
  Angle = 0
  AngleMax = 0
  AngleMin = 0
  Detach1 = false
  Detach2 = false
  Distance = 0
  Distance2 = 0
  EnableAngleMax = false
  EnableAngleMin = false
  EnableLengthMax = false
  EnableLengthMin = false
  JointType = 0 (Fixed)
  LengthMax = 0
  LengthMin = 0
  Placement1 = pos=(0,0,4) rot=(0,0,1;0rad)
  Placement2 = pos=(0,9e-16,4) rot=(1,0,0;3.14159rad)
  Reference1 = -> Assembly [bearing_holder.Face10,bearing_holder.Face10]
  Reference2 = -> Assembly [bearing_body.Face8,bearing_body.Face8]
  Suppressed = false
FEATURE [App::FeaturePython] Joint001  label="Fixed001"  # Assembly joint (typed FeaturePython)
  Angle = 0
  AngleMax = 0
  AngleMin = 0
  Detach1 = false
  Detach2 = false
  Distance = 0
  Distance2 = 0
  EnableAngleMax = false
  EnableAngleMin = false
  EnableLengthMax = false
  EnableLengthMin = false
  JointType = 0 (Fixed)
  LengthMax = 0
  LengthMin = 0
  Placement1 = pos=(0,0,0) rot=(1,0,0;3.14159rad)
  Placement2 = pos=(-7.1e-15,-3.2e-15,0) rot=(0,0,1;0rad)
  Reference1 = -> Assembly [bearing_body.Face7,bearing_body.Edge1]
  Reference2 = -> Assembly [bearing_holder.Face2,bearing_holder.Face2]
  Suppressed = false
FEATURE [App::Link] coil_frame  label="coil_frame001"
  LinkPlacement = pos=(7.5e-15,-4.7e-15,1e-16) rot=(0,0,1;3.14159rad)
  LinkedObject = -> Body012
  Placement = pos=(7.5e-15,-4.7e-15,1e-16) rot=(0,0,1;3.14159rad)
FEATURE [App::FeaturePython] Joint003  label="Fixed003"  # Assembly joint (typed FeaturePython)
  Angle = 0
  AngleMax = 0
  AngleMin = 0
  Detach1 = false
  Detach2 = false
  Distance = 0
  Distance2 = 0
  EnableAngleMax = false
  EnableAngleMin = false
  EnableLengthMax = false
  EnableLengthMin = false
  JointType = 0 (Fixed)
  LengthMax = 0
  LengthMin = 0
  Offset2 = pos=(0,0,0) rot=(0,0,-1;3.14159rad)
  Placement1 = pos=(16.6924,2.72749e-06,4) rot=(0,0,1;0rad)
  Placement2 = pos=(-16.6924,-2.72749e-06,4) rot=(0,0,-1;3.14159rad)
  Reference1 = -> Assembly [coil_frame.Face8,coil_frame.Face8]
  Reference2 = -> Assembly [bearing_holder.Face7,bearing_holder.Face7]
  Suppressed = false
FEATURE [App::Link] coil  label="coil001"
  LinkPlacement = pos=(-6.22e-14,-2.39e-14,35) rot=(0,1,0;3.14159rad)
  LinkedObject = -> Body013
  Placement = pos=(-6.22e-14,-2.39e-14,35) rot=(0,1,0;3.14159rad)
FEATURE [App::Link] coil001  label="coil002"
  LinkPlacement = pos=(-5.57e-14,-3.26e-14,35) rot=(1,0,0;3.14159rad)
  LinkedObject = -> Body013
  Placement = pos=(-5.57e-14,-3.26e-14,35) rot=(1,0,0;3.14159rad)
FEATURE [App::FeaturePython] Joint007  label="Revolute"  # Assembly joint (typed FeaturePython)
  Angle = 0
  AngleMax = 0
  AngleMin = 0
  Detach1 = false
  Detach2 = false
  Distance = 0
  Distance2 = 0
  EnableAngleMax = false
  EnableAngleMin = false
  EnableLengthMax = false
  EnableLengthMin = false
  JointType = 1 (Revolute)
  LengthMax = 0
  LengthMin = 0
  Offset1 = pos=(0,0,0) rot=(0,1,0;3.14159rad)
  Placement1 = pos=(0,0,0) rot=(0,0,1;3.14159rad)
  Placement2 = pos=(0,0,0) rot=(1,0,0;3.14159rad)
  Reference1 = -> Assembly [rotor.Edge39,rotor.Edge39]
  Reference2 = -> Assembly [bearing_body.Edge12,bearing_body.Edge12]
  Suppressed = false
FEATURE [Part::Sphere] Sphere010  label="ball"
  Angle1 = -90
  Angle2 = 90
  Angle3 = 360
  AttacherType = Attacher::AttachEngine3D
  AttachmentOffset = pos=(0,0,3) rot=(0,0,1;0rad)
  Placement = pos=(0,0,3.5) rot=(0,0,1;0rad)
  Radius = 3
  expr: .AttachmentOffset.Base.z = Spreadsheet.bearing_ball_radius
  expr: Radius = Spreadsheet.bearing_ball_radius
FEATURE [Sketcher::SketchObject] Sketch066
  ArcFitTolerance = 1e-06
  AttachmentSupport = -> [DatumPlane004]
  ExternalGeometry = -> [Revolution]
  ExternalTypes = [0]
  FullyConstrained = true
  MakeInternals = false
  MapMode = 5
  Placement = pos=(5,0,35) rot=(0.57735,0.57735,0.57735;2.0944rad)
  sketch-geometry (7):
    g0: LineSegment [constr] StartX=-3.5 StartY=-8 StartZ=0 EndX=-3.5 EndY=-27 EndZ=0
    g1: LineSegment [constr] StartX=3.5 StartY=-8 StartZ=0 EndX=3.5 EndY=-27 EndZ=0
    g2: LineSegment [constr] StartX=-3.5 StartY=-17.5 StartZ=0 EndX=3.5 EndY=-17.5 EndZ=0
    g3: GeomPoint [constr] X=1e-16 Y=-17.5 Z=0
    g4: LineSegment [constr] StartX=1e-16 StartY=-17.5 StartZ=0 EndX=0 EndY=-8 EndZ=0
    g5: LineSegment [constr] StartX=1e-16 StartY=-17.5 StartZ=0 EndX=-7e-16 EndY=-27 EndZ=0
    g6: Circle CenterX=0 CenterY=-12.75 CenterZ=0 NormalX=0 NormalY=0 NormalZ=1 AngleXU=0 Radius=3.2
  constraints (15):
    c: Coincident(g0,g-3)
    c: PointOnObject(g0,g-4)
    c: Vertical(g0)
    c: Coincident(g1,g-3)
    c: PointOnObject(g1,g-4)
    c: Vertical(g1)
    c: Symmetric(g0,g0,g2)
    c: Symmetric(g1,g1,g2)
    c: Symmetric(g2,g2,g3)
    c: Coincident(g4,g3)
    c: Symmetric(g-3,g-3,g4)
    c: Coincident(g5,g3)
    c: Symmetric(g-4,g-4,g5)
    c: Diameter(g6) = 6.4
    c: Symmetric(g4,g4,g6)
FEATURE [PartDesign::Pocket] Pocket
  BaseFeature = -> Revolution
  Direction = (-1,0,0)
  Length = 3.4
  Length2 = 5
  Profile = -> Sketch066
  ReferenceAxis = -> Sketch066 [N_Axis]
  Refine = true
  SideType = 0
  Suppressed = false
  Type = 0
  Type2 = 0
FEATURE [Sketcher::SketchObject] Sketch067
  ArcFitTolerance = 1e-06
  AttachmentSupport = -> [DatumPlane]
  ExternalGeometry = -> [Pocket]
  ExternalTypes = [0]
  FullyConstrained = true
  MakeInternals = false
  MapMode = 5
  Placement = pos=(3e-16,5,35) rot=(0,0.707107,0.707107;3.14159rad)
  sketch-geometry (6):
    g0: LineSegment [constr] StartX=-3.5 StartY=-8 StartZ=0 EndX=-3.5 EndY=-27 EndZ=0
    g1: LineSegment [constr] StartX=3.5 StartY=-27 StartZ=0 EndX=3.5 EndY=-8 EndZ=0
    g2: LineSegment [constr] StartX=-3.5 StartY=-17.5 StartZ=0 EndX=3.5 EndY=-17.5 EndZ=0
    g3: LineSegment [constr] StartX=5e-16 StartY=-17.5 StartZ=0 EndX=0 EndY=-8 EndZ=0
    g4: LineSegment [constr] StartX=5e-16 StartY=-17.5 StartZ=0 EndX=0 EndY=-27 EndZ=0
    g5: Circle CenterX=3e-16 CenterY=-22.25 CenterZ=0 NormalX=0 NormalY=0 NormalZ=1 AngleXU=0 Radius=3.2
  constraints (14):
    c: Coincident(g0,g-4)
    c: PointOnObject(g0,g-3)
    c: PointOnObject(g1,g-3)
    c: Coincident(g1,g-4)
    c: Vertical(g1)
    c: Vertical(g0)
    c: Symmetric(g0,g0,g2)
    c: Symmetric(g1,g1,g2)
    c: Symmetric(g2,g2,g3)
    c: Symmetric(g-4,g-4,g3)
    c: Coincident(g4,g3)
    c: Symmetric(g-3,g-3,g4)
    c: Symmetric(g4,g4,g5)
    c: Diameter(g5) = 6.4
FEATURE [PartDesign::Pocket] Pocket025
  BaseFeature = -> Pocket
  Direction = (0,-1,2e-16)
  Length = 3.4
  Length2 = 5
  Profile = -> Sketch067
  ReferenceAxis = -> Sketch067 [N_Axis]
  Refine = true
  SideType = 0
  Suppressed = false
  Type = 0
  Type2 = 0
FEATURE [Sketcher::SketchObject] Sketch068
  ArcFitTolerance = 1e-06
  AttachmentSupport = -> [DatumPlane003]
  ExternalGeometry = -> [Pocket025]
  ExternalTypes = [0]
  FullyConstrained = true
  MakeInternals = false
  MapMode = 5
  Placement = pos=(-5,-1e-16,35) rot=(0.57735,-0.57735,-0.57735;2.0944rad)
  sketch-geometry (1):
    g0: Circle CenterX=0 CenterY=-12.75 CenterZ=0 NormalX=0 NormalY=0 NormalZ=1 AngleXU=0 Radius=3.2
  constraints (2):
    c: Coincident(g0,g-3)
    c: Equal(g0,g-3)
FEATURE [PartDesign::Pocket] Pocket026
  BaseFeature = -> Pocket025
  Direction = (1,0,0)
  Length = 3.4
  Length2 = 5
  Profile = -> Sketch068
  ReferenceAxis = -> Sketch068 [N_Axis]
  Refine = true
  SideType = 0
  Suppressed = false
  Type = 0
  Type2 = 0
FEATURE [Sketcher::SketchObject] Sketch069
  ArcFitTolerance = 1e-06
  AttachmentSupport = -> [DatumPlane002]
  ExternalGeometry = -> [Pocket026]
  ExternalTypes = [0]
  FullyConstrained = true
  MakeInternals = false
  MapMode = 5
  Placement = pos=(-3.305e-13,-5,35) rot=(1,0,0;1.5708rad)
  sketch-geometry (1):
    g0: Circle CenterX=0 CenterY=-22.25 CenterZ=0 NormalX=0 NormalY=0 NormalZ=1 AngleXU=0 Radius=3.2
  constraints (2):
    c: Coincident(g0,g-3)
    c: Equal(g0,g-3)
FEATURE [PartDesign::Pocket] Pocket027
  BaseFeature = -> Pocket026
  Direction = (6.62e-14,1,-2e-16)
  Length = 3.4
  Length2 = 5
  Profile = -> Sketch069
  ReferenceAxis = -> Sketch069 [N_Axis]
  Refine = true
  SideType = 0
  Suppressed = false
  Type = 0
  Type2 = 0
FEATURE [PartDesign::Pocket] Pocket021
  BaseFeature = -> Pocket027
  Direction = (0,0,-1)
  Length = 5
  Length2 = 5
  Profile = -> Sketch053
  ReferenceAxis = -> Sketch053 [N_Axis]
  Refine = true
  SideType = 0
  Suppressed = false
  Type = 1
  Type2 = 0
FEATURE [PartDesign::Pocket] Pocket016
  BaseFeature = -> Pocket021
  Direction = (0,0,-1)
  Length = 5
  Length2 = 5
  Profile = -> Sketch038
  ReferenceAxis = -> Sketch038 [N_Axis]
  Refine = true
  SideType = 0
  Suppressed = false
  Type = 1
  Type2 = 0
FEATURE [PartDesign::Body] Body  label="rotor"
  AllowCompound = false
  Group = -> [Sketch,Pad,Sketch019,Pocket007,Sketch031,DatumPlane002,DatumPlane,DatumPlane003,DatumPlane004,Sketch034,Revolution,Sketch066,Pocket,Sketch067,Pocket025,Sketch068,Pocket026,Sketch069,Pocket027,Pocket021,Pocket016,Sketch038,Sketch053]
  Origin = -> Origin
  Tip = -> Pocket027
FEATURE [PartDesign::SubShapeBinder] Binder015
  BindCopyOnChange = 0
  BindMode = 0
  ClaimChildren = false
  Context = -> Body014 [Binder015.]
  Fuse = false
  MakeFace = true
  OffsetFill = false
  OffsetIntersection = false
  OffsetJoinType = 0
  OffsetOpenResult = false
  PartialLoad = false
  Refine = true
  Relative = true
  Support = -> [Body012]
  _Version = 2
FEATURE [PartDesign::SubShapeBinder] Binder016
  BindCopyOnChange = 0
  BindMode = 0
  ClaimChildren = false
  Context = -> Body014 [Binder016.]
  Fuse = false
  MakeFace = true
  OffsetFill = false
  OffsetIntersection = false
  OffsetJoinType = 0
  OffsetOpenResult = false
  PartialLoad = false
  Refine = true
  Relative = true
  Support = -> [Body011]
  _Version = 2
FEATURE [Sketcher::SketchObject] Sketch070
  ArcFitTolerance = 1e-06
  AttachmentSupport = -> [Binder016]
  ExternalGeometry = -> [Binder015,Binder016]
  ExternalTypes = [0]
  FullyConstrained = true
  MakeInternals = false
  MapMode = 5
  Placement = pos=(0,0,8) rot=(0,0,1;0rad)
  sketch-geometry (6):
    g0: GeomPoint X=-12.5 Y=-3.57071 Z=0
    g1: GeomPoint X=12.5 Y=-3.57071 Z=0
    g2: ArcOfCircle CenterX=1.67194e-11 CenterY=0 CenterZ=0 NormalX=0 NormalY=0 NormalZ=1 AngleXU=0 Radius=13 StartAngle=3.41984 EndAngle=6.00494
    g3: ArcOfCircle CenterX=1.67194e-11 CenterY=0 CenterZ=0 NormalX=0 NormalY=0 NormalZ=1 AngleXU=0 Radius=17 StartAngle=3.88629 EndAngle=5.53849
    g4: LineSegment StartX=-12.5 StartY=-11.5217 StartZ=0 EndX=-12.5 EndY=-3.57071 EndZ=0
    g5: LineSegment StartX=12.5 StartY=-11.5217 StartZ=0 EndX=12.5 EndY=-3.57071 EndZ=0
  constraints (13):
    c: PointOnObject(g0,g-4)
    c: PointOnObject(g0,g-3)
    c: PointOnObject(g1,g-7)
    c: Coincident(g3,g2)
    c: Coincident(g3,g-5)
    c: Coincident(g3,g-7)
    c: Coincident(g4,g3)
    c: Coincident(g4,g0)
    c: Coincident(g5,g3)
    c: Coincident(g5,g1)
    c: Coincident(g2,g1)
    c: Coincident(g2,g0)
    c: Coincident(g2,g-4)
FEATURE [PartDesign::Pad] Pad026
  Direction = (0,0,1)
  Length = 10
  Length2 = 10
  Profile = -> Sketch070
  ReferenceAxis = -> Sketch070 [N_Axis]
  Refine = true
  SideType = 0
  Suppressed = false
  Type = 3
  Type2 = 0
  UpToFace = -> Binder015 [Face11]
FEATURE [PartDesign::Mirrored] Mirrored
  BaseFeature = -> Pad026
  MirrorPlane = -> XZ_Plane015
  Originals = -> [Pad026]
  Refine = true
  Suppressed = false
  TransformMode = 0
FEATURE [Sketcher::SketchObject] Sketch071
  ArcFitTolerance = 1e-06
  AttachmentSupport = -> [Mirrored]
  ExternalGeometry = -> [Binder015,Binder016]
  ExternalTypes = [0]
  FullyConstrained = true
  MakeInternals = false
  MapMode = 5
  Placement = pos=(0,0,20) rot=(0,0,1;0rad)
  sketch-geometry (4):
    g0: Circle CenterX=0 CenterY=0 CenterZ=0 NormalX=0 NormalY=0 NormalZ=1 AngleXU=0 Radius=20
    g1: Circle CenterX=0 CenterY=0 CenterZ=0 NormalX=0 NormalY=0 NormalZ=1 AngleXU=0 Radius=13
    g2: GeomPoint X=0 Y=-13 Z=0
    g3: GeomPoint X=0 Y=-13 Z=0
  constraints (7):
    c: Coincident(g0,g-1)
    c: Tangent(g0,g-3)
    c: Coincident(g1,g0)
    c: PointOnObject(g2,g-4)
    c: PointOnObject(g3,g1)
    c: Coincident(g2,g3)
    c: PointOnObject(g2,g-2)
FEATURE [PartDesign::Pad] Pad027
  BaseFeature = -> Mirrored
  Direction = (0,0,1)
  Length = 10
  Length2 = 10
  Profile = -> Sketch071
  ReferenceAxis = -> Sketch071 [N_Axis]
  Refine = true
  SideType = 0
  Suppressed = false
  Type = 0
  Type2 = 0
FEATURE [PartDesign::Mirrored] Mirrored001
  BaseFeature = -> Pad027
  MirrorPlane = -> XZ_Plane015
  Originals = -> [Pad026]
  Refine = true
  Suppressed = false
  TransformMode = 0
FEATURE [PartDesign::Body] Body014  label="encoder"
  AllowCompound = false
  Group = -> [Binder016,Binder015,Sketch070,Pad026,Mirrored,Sketch071,Pad027,Mirrored001]
  Origin = -> Origin015
  Tip = -> Mirrored001
FEATURE [App::Point] Origin017  label="Origin"
  Role = Origin
FEATURE [App::Point] Origin018  label="Origin"
  Role = Origin
FEATURE [App::Point] Origin019  label="Origin"
  Role = Origin
FEATURE [App::Point] Origin020  label="Origin"
  Role = Origin
FEATURE [App::Point] Origin021  label="Origin"
  Role = Origin
FEATURE [App::Point] Origin022  label="Origin"
  Role = Origin
FEATURE [App::Point] Origin024  label="Origin"
  Role = Origin
FEATURE [Spreadsheet::Sheet] Spreadsheet
  cells = A1='Bearing ball radius; B1(bearing_ball_radius)==3 mm; A2='Bearing radius extra play; B2(bearing_ball_radius_extra_play)==0 mm; A3='Number of balls; B3(number_of_balls)=4
FEATURE [PartDesign::SubShapeBinder] Binder017
  BindCopyOnChange = 0
  BindMode = 0
  ClaimChildren = false
  Context = -> Part001 [Binder017.]
  Fuse = false
  MakeFace = true
  OffsetFill = false
  OffsetIntersection = false
  OffsetJoinType = 0
  OffsetOpenResult = false
  PartialLoad = false
  Refine = true
  Relative = true
  Support = -> [Body007,Binder018]
  _Version = 2
FEATURE [PartDesign::SubShapeBinder] Binder018
  BindCopyOnChange = 0
  BindMode = 0
  ClaimChildren = false
  Context = -> Part001 [Binder018.]
  Fuse = false
  MakeFace = true
  OffsetFill = false
  OffsetIntersection = false
  OffsetJoinType = 0
  OffsetOpenResult = false
  PartialLoad = false
  Refine = true
  Relative = true
  Support = -> [Body]
  _Version = 2
FEATURE [Sketcher::SketchObject] Sketch073  label="reference2"
  ArcFitTolerance = 1e-06
  AttachmentSupport = -> [Origin027]
  ExternalGeometry = -> [Binder018,Binder017]
  ExternalTypes = [0,0]
  FullyConstrained = true
  MakeInternals = false
  MapMode = 5
  sketch-geometry (2):
    g0: Circle CenterX=0 CenterY=1.8e-15 CenterZ=0 NormalX=0 NormalY=0 NormalZ=1 AngleXU=0 Radius=7.5
    g1: Circle CenterX=0 CenterY=1.8e-15 CenterZ=0 NormalX=0 NormalY=0 NormalZ=1 AngleXU=0 Radius=9.7
  constraints (6):
    c: Coincident(g0,g-4)
    c: Coincident(g1,g0)
    c: Distance(g0,g-3) = 0.5
    c: Distance(g1,g-4) = 0.3
    c: Diameter(g1) = 19.4  'OuterDiameter'
    c: Diameter(g0) = 15  'InnerDiameter'
FEATURE [Sketcher::SketchObject] Sketch074  label="reference1"
  ArcFitTolerance = 1e-06
  AttachmentSupport = -> [Origin027]
  ExternalGeometry = -> [Binder017]
  ExternalTypes = [0]
  FullyConstrained = true
  MakeInternals = false
  MapMode = 5
  Placement = pos=(0,0,0) rot=(1,0,0;1.5708rad)
  constraints (1):
    c: DistanceY(g-3,g-3) = 8  'BearingHeight'
FEATURE [App::Point] Origin028  label="Origin029"
  Role = Origin
FEATURE [Part::FeaturePython] PolarArray  # WARN: FeaturePython — macro-defined, semantics opaque (R4)
  Alignment = 0
  AttacherType = Attacher::AttachEngine3D
  CellStart = A1
  Count = 4
  DistributionLaw = 0
  EndInclusive = false
  ExposePlacement = false
  FlipX = false
  FlipZ = false
  GeneratorMode = 0
  MarkerShape = 1
  MarkerSize = 2
  NumElements = 4
  OrientMode = 2
  Radius = 0
  Reverse = false
  SpanEnd = 360
  SpanStart = 0
  Step = 90
  Type = lattice2PolarArray2.PolarArray
  UseArcRadius = false
  UseArcRange = 0
  VSGVersion = 1
  Values = 0.0 | 90.0 | 180.0 | 270.0
  ValuesSource = 2
  isLattice = 1
  expr: Count = Spreadsheet.number_of_balls
FEATURE [Part::Extrusion] Extrude
  Base = -> Sketch073
  Dir = (0,0,1)
  DirMode = 2
  FaceMakerClass = Part::FaceMakerBullseye
  FaceMakerMode = 3
  LengthFwd = 8
  LengthRev = 0
  Solid = true
  Symmetric = false
  expr: LengthFwd = <<reference1>>.Constraints.BearingHeight
FEATURE [Sketcher::SketchObject] Mapped_Sketch002
  ArcFitTolerance = 1e-06
  AttachmentSupport = -> [Extrude]
  ExternalTypes = [0]
  FullyConstrained = true
  MakeInternals = false
  MapMode = 45
  Placement = pos=(0,1.6e-15,4) rot=(0,0,1;0rad)
  expr: Constraints[21] = Sketch073.Constraints.OuterDiameter * 3.14159265 / Spreadsheet.number_of_balls
  expr: Constraints[7] = Sketch073.Constraints.OuterDiameter * 3.14159265
  expr: Constraints[8] = <<reference1>>.Constraints.BearingHeight
  sketch-geometry (33):
    g0: LineSegment [constr] StartX=0 StartY=0 StartZ=0 EndX=60.9469 EndY=0 EndZ=0
    g1: LineSegment [constr] StartX=60.9469 StartY=0 StartZ=0 EndX=60.9469 EndY=8 EndZ=0
    g2: LineSegment [constr] StartX=60.9469 StartY=8 StartZ=0 EndX=0 EndY=8 EndZ=0
    g3: LineSegment [constr] StartX=0 StartY=8 StartZ=0 EndX=0 EndY=0 EndZ=0
    g4: ArcOfCircle CenterX=7.61836 CenterY=4 CenterZ=0 NormalX=0 NormalY=0 NormalZ=1 AngleXU=0 Radius=3.3 StartAngle=5.49779 EndAngle=10.2102
    g5: LineSegment [constr] StartX=5.28491 StartY=1.66655 StartZ=0 EndX=9.95181 EndY=1.66655 EndZ=0
    g6: GeomPoint [constr] X=7.61836 Y=4 Z=0
    g7: LineSegment [constr] StartX=7.61836 StartY=4 StartZ=0 EndX=9.95181 EndY=1.66655 EndZ=0
    g8: LineSegment [constr] StartX=7.61836 StartY=4 StartZ=0 EndX=7.61836 EndY=7.3 EndZ=0
    g9: LineSegment [constr] StartX=0 StartY=8 StartZ=0 EndX=15.2367 EndY=8 EndZ=0
    g10: LineSegment [constr] StartX=15.2367 StartY=8 StartZ=0 EndX=15.2367 EndY=0 EndZ=0
    g11: GeomPoint [constr] X=0 Y=4 Z=0
    g12: GeomPoint [constr] X=15.2367 Y=4 Z=0
    g13: LineSegment [constr] StartX=0 StartY=4 StartZ=0 EndX=15.2367 EndY=4 EndZ=0
    g14: GeomPoint [constr] X=7.61836 Y=4 Z=0
    g15: LineSegment StartX=5.28491 StartY=1.66655 StartZ=0 EndX=3.31836 EndY=1.04641 EndZ=0
    g16: LineSegment [constr] StartX=5.28491 StartY=1.66655 StartZ=0 EndX=7.61836 EndY=4 EndZ=0
    g17: LineSegment StartX=0 StartY=4 StartZ=0 EndX=0 EndY=8 EndZ=0
    g18: LineSegment StartX=0 StartY=8 StartZ=0 EndX=15.2367 EndY=8 EndZ=0
    g19: LineSegment StartX=15.2367 StartY=8 StartZ=0 EndX=15.2367 EndY=4 EndZ=0
    g20: LineSegment StartX=3.31836 StartY=1.04641 StartZ=0 EndX=3.31836 EndY=4 EndZ=0
    g21: LineSegment StartX=3.31836 StartY=4 StartZ=0 EndX=2.31836 EndY=4 EndZ=0
    g22: LineSegment StartX=2.31836 StartY=4 StartZ=0 EndX=2.31836 EndY=0.731074 EndZ=0
    g23: LineSegment StartX=2.31836 StartY=0.731074 StartZ=0 EndX=0 EndY=0 EndZ=0
    g24: LineSegment StartX=0 StartY=0 StartZ=0 EndX=0 EndY=4 EndZ=0
    g25: LineSegment StartX=12.9184 StartY=0.731074 StartZ=0 EndX=12.9184 EndY=4 EndZ=0
    g26: LineSegment StartX=12.9184 StartY=4 StartZ=0 EndX=11.9184 EndY=4 EndZ=0
    g27: LineSegment StartX=11.9184 StartY=4 StartZ=0 EndX=11.9184 EndY=1.04641 EndZ=0
    g28: LineSegment [constr] StartX=2.31836 StartY=0.731074 StartZ=0 EndX=3.31836 EndY=1.04641 EndZ=0
    g29: LineSegment [constr] StartX=11.9184 StartY=1.04641 StartZ=0 EndX=12.9184 EndY=0.731074 EndZ=0
    g30: LineSegment StartX=9.95181 StartY=1.66655 StartZ=0 EndX=11.9184 EndY=1.04641 EndZ=0
    g31: LineSegment StartX=12.9184 StartY=0.731074 StartZ=0 EndX=15.2367 EndY=0 EndZ=0
    g32: LineSegment StartX=15.2367 StartY=0 StartZ=0 EndX=15.2367 EndY=4 EndZ=0
  constraints (78):
    c: Coincident(g0,g1)
    c: Coincident(g1,g2)
    c: Coincident(g2,g3)
    c: Horizontal(g0)
    c: Horizontal(g2)
    c: Vertical(g1)
    c: Vertical(g3)
    c: DistanceX(g2,g2) = 60.9469
    c: DistanceY(g1,g1) = 8
    c: Radius(g4) = 3.3
    c: Angle(g4) = 4.71239
    c: Coincident(g5,g4)
    c: Coincident(g5,g4)
    c: Horizontal(g5)
    c: Coincident(g4,g6)
    c: Coincident(g7,g4)
    c: Coincident(g7,g4)
    c: PointOnObject(g8,g4)
    c: Coincident(g8,g4)
    c: Vertical(g8)
    c: Horizontal(g9)
    c: Distance(g9,g9) = 15.2367
    c: Coincident(g0,g3)
    c: Coincident(g0,g-1)
    c: Coincident(g9,g2)
    c: Coincident(g10,g9)
    c: PointOnObject(g10,g0)
    c: Vertical(g10)
    c: Symmetric(g3,g3,g11)
    c: Symmetric(g10,g10,g12)
    c: Coincident(g13,g11)
    c: Coincident(g13,g12)
    c: Symmetric(g13,g13,g14)
    c: Coincident(g4,g14)
    c: Coincident(g15,g4)
    c: Coincident(g16,g4)
    c: Coincident(g16,g4)
    c: Coincident(g17,g11)
    c: Coincident(g17,g2)
    c: Coincident(g18,g2)
    c: Coincident(g18,g9)
    c: Coincident(g19,g9)
    c: Coincident(g19,g12)
    c: Coincident(g20,g15)
    c: PointOnObject(g20,g13)
    c: Vertical(g20)
    c: Coincident(g21,g20)
    c: PointOnObject(g21,g13)
    c: Coincident(g22,g21)
    c: Vertical(g22)
    c: Coincident(g23,g22)
    c: Coincident(g23,g0)
    c: Coincident(g24,g0)
    c: Coincident(g24,g11)
    c: PointOnObject(g25,g13)
    c: Vertical(g25)
    c: Coincident(g26,g25)
    c: PointOnObject(g26,g13)
    c: Coincident(g27,g26)
    c: Vertical(g27)
    c: Coincident(g28,g22)
    c: Coincident(g28,g15)
    c: Coincident(g29,g27)
    c: Coincident(g29,g25)
    c: Parallel(g23,g28)
    c: Parallel(g28,g15)
    c: Coincident(g30,g4)
    c: Coincident(g30,g27)
    c: Coincident(g31,g25)
    c: Coincident(g31,g10)
    c: Parallel(g31,g30)
    c: Parallel(g30,g29)
    c: Equal(g15,g30)
    c: Equal(g23,g31)
    c: Distance(g21,g21) = 1
    c: Distance(g20,g4) = 1
    c: Coincident(g32,g10)
    c: Coincident(g32,g12)
FEATURE [Sketcher::SketchObject] Mapped_Sketch003
  ArcFitTolerance = 1e-06
  AttachmentSupport = -> [Extrude]
  ExternalTypes = [0]
  FullyConstrained = true
  MakeInternals = false
  MapMode = 45
  Placement = pos=(9e-16,2e-15,4) rot=(0,0,1;0rad)
  expr: Constraints[20] = Sketch073.Constraints.InnerDiameter * 3.14159265 / Spreadsheet.number_of_balls
  expr: Constraints[6] = Sketch073.Constraints.InnerDiameter * 3.14159265
  expr: Constraints[7] = <<reference1>>.Constraints.BearingHeight
  sketch-geometry (33):
    g0: LineSegment [constr] StartX=47.1239 StartY=0 StartZ=0 EndX=47.1239 EndY=8 EndZ=0
    g1: LineSegment [constr] StartX=47.1239 StartY=8 StartZ=0 EndX=0 EndY=8 EndZ=0
    g2: LineSegment [constr] StartX=0 StartY=8 StartZ=0 EndX=0 EndY=0 EndZ=0
    g3: ArcOfCircle CenterX=5.89049 CenterY=4 CenterZ=0 NormalX=0 NormalY=0 NormalZ=1 AngleXU=0 Radius=3.3 StartAngle=5.49779 EndAngle=10.2102
    g4: LineSegment [constr] StartX=3.55703 StartY=1.66655 StartZ=0 EndX=8.22394 EndY=1.66655 EndZ=0
    g5: GeomPoint [constr] X=5.89049 Y=4 Z=0
    g6: LineSegment [constr] StartX=5.89049 StartY=4 StartZ=0 EndX=8.22394 EndY=1.66655 EndZ=0
    g7: LineSegment [constr] StartX=5.89049 StartY=4 StartZ=0 EndX=5.89049 EndY=7.3 EndZ=0
    g8: LineSegment [constr] StartX=0 StartY=8 StartZ=0 EndX=11.781 EndY=8 EndZ=0
    g9: LineSegment [constr] StartX=11.781 StartY=8 StartZ=0 EndX=11.781 EndY=0 EndZ=0
    g10: GeomPoint [constr] X=5.89049 Y=4 Z=0
    g11: LineSegment [constr] StartX=3.55703 StartY=1.66655 StartZ=0 EndX=5.89049 EndY=4 EndZ=0
    g12: GeomPoint [constr] X=0 Y=4 Z=0
    g13: GeomPoint [constr] X=11.781 Y=4 Z=0
    g14: LineSegment [constr] StartX=0 StartY=4 StartZ=0 EndX=11.781 EndY=4 EndZ=0
    g15: GeomPoint [constr] X=5.89049 Y=4 Z=0
    g16: LineSegment StartX=1.59049 StartY=0.745177 StartZ=0 EndX=3.55703 EndY=1.66655 EndZ=0
    g17: LineSegment StartX=8.22394 StartY=1.66655 StartZ=0 EndX=10.1905 EndY=0.745177 EndZ=0
    g18: LineSegment StartX=0 StartY=4 StartZ=0 EndX=0 EndY=8 EndZ=0
    g19: LineSegment StartX=0 StartY=8 StartZ=0 EndX=11.781 EndY=8 EndZ=0
    g20: LineSegment StartX=11.781 StartY=8 StartZ=0 EndX=11.781 EndY=4 EndZ=0
    g21: LineSegment StartX=1.59049 StartY=0.745177 StartZ=0 EndX=1.59049 EndY=4 EndZ=0
    g22: LineSegment StartX=1.59049 StartY=4 StartZ=0 EndX=0.590486 EndY=4 EndZ=0
    g23: LineSegment StartX=0.590486 StartY=4 StartZ=0 EndX=0.590486 EndY=0.276656 EndZ=0
    g24: LineSegment StartX=0.590486 StartY=0.276656 StartZ=0 EndX=0 EndY=0 EndZ=0
    g25: LineSegment StartX=0 StartY=0 StartZ=0 EndX=0 EndY=4 EndZ=0
    g26: LineSegment [constr] StartX=0.590486 StartY=0.276656 StartZ=0 EndX=1.59049 EndY=0.745177 EndZ=0
    g27: LineSegment StartX=10.1905 StartY=0.745177 StartZ=0 EndX=10.1905 EndY=4 EndZ=0
    g28: LineSegment StartX=10.1905 StartY=4 StartZ=0 EndX=11.1905 EndY=4 EndZ=0
    g29: LineSegment StartX=11.1905 StartY=4 StartZ=0 EndX=11.1905 EndY=0.276656 EndZ=0
    g30: LineSegment StartX=11.1905 StartY=0.276656 StartZ=0 EndX=11.781 EndY=0 EndZ=0
    g31: LineSegment [constr] StartX=11.1905 StartY=0.276656 StartZ=0 EndX=10.1905 EndY=0.745177 EndZ=0
    g32: LineSegment StartX=11.781 StartY=0 StartZ=0 EndX=11.781 EndY=4 EndZ=0
  constraints (77):
    c: Coincident(g0,g1)
    c: Coincident(g1,g2)
    c: Coincident(g2,g-1)
    c: Horizontal(g1)
    c: Vertical(g0)
    c: Vertical(g2)
    c: DistanceX(g1,g1) = 47.1239
    c: DistanceY(g0,g0) = 8
    c: Radius(g3) = 3.3
    c: Angle(g3) = 4.71239
    c: Coincident(g4,g3)
    c: Coincident(g4,g3)
    c: Horizontal(g4)
    c: Coincident(g3,g5)
    c: Coincident(g6,g3)
    c: Coincident(g6,g3)
    c: PointOnObject(g7,g3)
    c: Coincident(g7,g3)
    c: Vertical(g7)
    c: Horizontal(g8)
    c: Distance(g8,g8) = 11.781
    c: Coincident(g9,g8)
    c: Vertical(g9)
    c: Coincident(g3,g10)
    c: Coincident(g11,g3)
    c: Coincident(g11,g3)
    c: Coincident(g8,g1)
    c: Symmetric(g2,g2,g12)
    c: Symmetric(g9,g9,g13)
    c: Coincident(g14,g12)
    c: Coincident(g14,g13)
    c: Symmetric(g14,g14,g15)
    c: Coincident(g15,g3)
    c: Coincident(g16,g3)
    c: Coincident(g17,g3)
    c: Equal(g17,g16)
    c: Coincident(g18,g12)
    c: Coincident(g18,g1)
    c: Coincident(g19,g1)
    c: Coincident(g19,g8)
    c: Coincident(g20,g8)
    c: Coincident(g20,g13)
    c: PointOnObject(g9,g-1)
    c: PointOnObject(g0,g-1)
    c: Coincident(g21,g16)
    c: PointOnObject(g21,g14)
    c: Vertical(g21)
    c: Coincident(g22,g21)
    c: PointOnObject(g22,g14)
    c: Coincident(g23,g22)
    c: Vertical(g23)
    c: Coincident(g24,g23)
    c: Coincident(g24,g2)
    c: Coincident(g25,g2)
    c: Coincident(g25,g12)
    c: Distance(g21,g3) = 1
    c: Coincident(g26,g23)
    c: Coincident(g26,g16)
    c: Parallel(g24,g26)
    c: Parallel(g26,g16)
    c: DistanceX(g22,g22) = 1
    c: Coincident(g27,g17)
    c: PointOnObject(g27,g14)
    c: Vertical(g27)
    c: Coincident(g28,g27)
    c: PointOnObject(g28,g14)
    c: Coincident(g29,g28)
    c: Vertical(g29)
    c: Coincident(g30,g29)
    c: Coincident(g30,g9)
    c: Coincident(g31,g29)
    c: Coincident(g31,g17)
    c: Equal(g30,g24)
    c: Parallel(g31,g30)
    c: Parallel(g30,g17)
    c: Coincident(g32,g9)
    c: Coincident(g32,g13)
FEATURE [Part::FeaturePython] Sketch_On_Surface002  label="map_outer007"  # WARN: FeaturePython — macro-defined, semantics opaque (R4)
  ConstructionBounds = true
  FillExtrusion = false
  FillFaces = true
  ReverseU = false
  ReverseV = true
  Sketch = -> Mapped_Sketch002
  SwapUV = false
  Thickness = 0
FEATURE [Part::FeaturePython] Sketch_On_Surface003  label="map_inner007"  # WARN: FeaturePython — macro-defined, semantics opaque (R4)
  ConstructionBounds = true
  FillExtrusion = false
  FillFaces = true
  ReverseU = false
  ReverseV = true
  Sketch = -> Mapped_Sketch003
  SwapUV = false
  Thickness = 0
FEATURE [Part::Loft] Loft
  Closed = false
  MaxDegree = 5
  Ruled = false
  Sections = -> [Sketch_On_Surface003,Sketch_On_Surface002]
  Solid = true
FEATURE [Part::FeaturePython] Populate  label="Populate PolarArray with Loft001"  # WARN: FeaturePython — macro-defined, semantics opaque (R4)
  Copying = 0
  ExposePlacement = false
  MarkerShape = 1
  MarkerSize = 0
  NumElements = 0
  Object = -> Loft
  OutputCompounding = 1
  PlacementsTo = -> PolarArray
  Referencing = 1
  Type = lattice2PopulateCopies.LatticePopulateCopies
  isLattice = 0
FEATURE [App::Link] fused_crown  label="crown001"
  LinkedObject = -> Common
FEATURE [App::FeaturePython] Move004  label="Move007"  # WARN: FeaturePython — macro-defined, semantics opaque (R4)
  MoveType = 0
  MovementTransform = pos=(0,0,-11) rot=(0,0,1;0rad)
  References = -> Assembly [bearing_body.]
FEATURE [App::FeaturePython] Move005  label="Move008"  # WARN: FeaturePython — macro-defined, semantics opaque (R4)
  MoveType = 0
  MovementTransform = pos=(0,0,7) rot=(0,0,1;0rad)
  References = -> Assembly [fused_crown.]
FEATURE [App::FeaturePython] Move  label="Move009"  # WARN: FeaturePython — macro-defined, semantics opaque (R4)
  MoveType = 1
  MovementTransform = pos=(-28.9917,0.69265,0) rot=(0,0,-1.00436;0rad)
  References = -> Assembly [rotor.,bearing_body.,bearing_holder.,coil_frame.,coil.,coil001.,fused_crown.]
FEATURE [App::FeaturePython] Move006  label="Move010"  # WARN: FeaturePython — macro-defined, semantics opaque (R4)
  MoveType = 0
  MovementTransform = pos=(0,0,-8) rot=(0,0,1;0rad)
  References = -> Assembly [fused_crown.]
FEATURE [App::FeaturePython] Move007  label="Move011"  # WARN: FeaturePython — macro-defined, semantics opaque (R4)
  MoveType = 0
  MovementTransform = pos=(0,0,15) rot=(0,0,1;0rad)
  References = -> Assembly [bearing_body.]
FEATURE [App::FeaturePython] Move008  label="Move012"  # WARN: FeaturePython — macro-defined, semantics opaque (R4)
  MoveType = 0
  MovementTransform = pos=(0,0,17) rot=(0,0,1;0rad)
  References = -> Assembly [bearing_body.]
FEATURE [App::FeaturePython] Move009  label="Move013"  # WARN: FeaturePython — macro-defined, semantics opaque (R4)
  MoveType = 0
  MovementTransform = pos=(0,0,-17) rot=(0,0,1;0rad)
  References = -> Assembly [bearing_holder.]
FEATURE [App::FeaturePython] Move010  label="Move014"  # WARN: FeaturePython — macro-defined, semantics opaque (R4)
  MoveType = 0
  MovementTransform = pos=(0,0,-4) rot=(0,0,1;0rad)
  References = -> Assembly [bearing_body.]
FEATURE [App::FeaturePython] Exploded_View  # WARN: FeaturePython — macro-defined, semantics opaque (R4)
  Group = -> [Move004,Move005,Move,Move006,Move007,Move008,Move009,Move010]
FEATURE [Assembly::ViewGroup] Exploded_Views
  Group = -> [Exploded_View]
FEATURE [Part::MultiFuse] Fusion  label="fused_crown"
  Refine = true
  Shapes = -> [Populate]
FEATURE [App::FeaturePython] Joint008  label="Fixed012"  # Assembly joint (typed FeaturePython)
  Angle = 0
  AngleMax = 0
  AngleMin = 0
  Detach1 = false
  Detach2 = false
  Distance = 0
  Distance2 = 0
  EnableAngleMax = false
  EnableAngleMin = false
  EnableLengthMax = false
  EnableLengthMin = false
  JointType = 0 (Fixed)
  LengthMax = 0
  LengthMin = 0
  Offset2 = pos=(0,0,-20) rot=(0,0,1;0rad)
  Placement1 = pos=(20,0,17.5) rot=(0.57735,0.57735,0.57735;2.0944rad)
  Placement2 = pos=(20,-1.2e-15,17.5) rot=(0.57735,-0.57735,-0.57735;2.0944rad)
  Reference1 = -> Assembly [coil.Face14,coil.Edge5]
  Reference2 = -> Assembly [coil_frame.Face17,coil_frame.Edge3]
  Suppressed = false
FEATURE [App::FeaturePython] Joint009  label="Fixed013"  # Assembly joint (typed FeaturePython)
  Angle = 0
  AngleMax = 0
  AngleMin = 0
  Detach1 = false
  Detach2 = false
  Distance = 0
  Distance2 = 0
  EnableAngleMax = false
  EnableAngleMin = false
  EnableLengthMax = false
  EnableLengthMin = false
  JointType = 0 (Fixed)
  LengthMax = 0
  LengthMin = 0
  Offset2 = pos=(0,0,-20) rot=(0,0,1;0rad)
  Placement1 = pos=(20,0,17.5) rot=(-0.57735,-0.57735,-0.57735;4.18879rad)
  Placement2 = pos=(-20,-5e-16,17.5) rot=(-0.57735,-0.57735,-0.57735;4.18879rad)
  Reference1 = -> Assembly [coil001.Face14,coil001.Edge5]
  Reference2 = -> Assembly [coil_frame.Face16,coil_frame.Edge4]
  Suppressed = false
FEATURE [App::Link] magnet  label="magnet001"
  LinkPlacement = pos=(1.13379,-1.12894,22.25) rot=(0.678761,-0.2803,0.678761;2.59502rad)
  LinkedObject = -> Cylinder001
  Placement = pos=(1.13379,-1.12894,22.25) rot=(0.678761,-0.2803,0.678761;2.59502rad)
FEATURE [App::Link] magnet001  label="magnet002"
  LinkPlacement = pos=(-1.12894,-1.13379,12.75) rot=(0.358213,-0.862187,0.358213;1.71854rad)
  LinkedObject = -> Cylinder001
  Placement = pos=(-1.12894,-1.13379,12.75) rot=(0.358213,-0.862187,0.358213;1.71854rad)
FEATURE [App::Link] magnet002  label="magnet003"
  LinkPlacement = pos=(-3.40138,3.38683,22.25) rot=(0.678761,-0.2803,0.678761;2.59502rad)
  LinkedObject = -> Cylinder001
  Placement = pos=(-3.40138,3.38683,22.25) rot=(0.678761,-0.2803,0.678761;2.59502rad)
FEATURE [App::Link] magnet003  label="magnet004"
  LinkPlacement = pos=(1.12894,1.13379,12.75) rot=(0.2803,0.678761,0.678761;2.59502rad)
  LinkedObject = -> Cylinder001
  Placement = pos=(1.12894,1.13379,12.75) rot=(0.2803,0.678761,0.678761;2.59502rad)
FEATURE [App::FeaturePython] Joint010  label="Fixed015"  # Assembly joint (typed FeaturePython)
  Angle = 0
  AngleMax = 0
  AngleMin = 0
  Detach1 = false
  Detach2 = false
  Distance = 0
  Distance2 = 0
  EnableAngleMax = false
  EnableAngleMin = false
  EnableLengthMax = false
  EnableLengthMin = false
  JointType = 0 (Fixed)
  LengthMax = 0
  LengthMin = 0
  Placement1 = pos=(0,-3e-16,0) rot=(0,0,1;0rad)
  Placement2 = pos=(-1.6,7e-16,22.25) rot=(-0.707107,0,-0.707107;3.14159rad)
  Reference1 = -> Assembly [magnet.Face2,magnet.Face2]
  Reference2 = -> Assembly [rotor.Face13,rotor.Face13]
  Suppressed = false
FEATURE [App::FeaturePython] Joint011  label="Fixed017"  # Assembly joint (typed FeaturePython)
  Angle = 0
  AngleMax = 0
  AngleMin = 0
  Detach1 = false
  Detach2 = false
  Distance = 0
  Distance2 = 0
  EnableAngleMax = false
  EnableAngleMin = false
  EnableLengthMax = false
  EnableLengthMin = false
  JointType = 0 (Fixed)
  LengthMax = 0
  LengthMin = 0
  Offset1 = pos=(3.2,0,0) rot=(0,0,1;0rad)
  Placement1 = pos=(3.2,0,4e-16) rot=(0,0,1;0rad)
  Placement2 = pos=(3.2,-1.6,12.75) rot=(-1,0,0;1.5708rad)
  Reference1 = -> Assembly [magnet003.Face2,magnet003.Face2]
  Reference2 = -> Assembly [rotor.Face15,rotor.Vertex22]
  Suppressed = false
FEATURE [App::FeaturePython] Joint012  label="Fixed019"  # Assembly joint (typed FeaturePython)
  Angle = 0
  AngleMax = 0
  AngleMin = 0
  Detach1 = false
  Detach2 = false
  Distance = 0
  Distance2 = 0
  EnableAngleMax = false
  EnableAngleMin = false
  EnableLengthMax = false
  EnableLengthMin = false
  JointType = 0 (Fixed)
  LengthMax = 0
  LengthMin = 0
  Placement1 = pos=(0,0,3.2) rot=(0,0,1;0rad)
  Placement2 = pos=(1.6,-1.3e-15,22.25) rot=(-0.707107,0,-0.707107;3.14159rad)
  Reference1 = -> Assembly [magnet002.Face3,magnet002.Face3]
  Reference2 = -> Assembly [rotor.Face11,rotor.Face11]
  Suppressed = false
FEATURE [App::FeaturePython] Joint013  label="Fixed020"  # Assembly joint (typed FeaturePython)
  Angle = 0
  AngleMax = 0
  AngleMin = 0
  Detach1 = false
  Detach2 = false
  Distance = 0
  Distance2 = 0
  EnableAngleMax = false
  EnableAngleMin = false
  EnableLengthMax = false
  EnableLengthMin = false
  JointType = 0 (Fixed)
  LengthMax = 0
  LengthMin = 0
  Offset2 = pos=(0,0,3.2) rot=(0,0,1;0rad)
  Placement1 = pos=(0,-2e-16,3.2) rot=(0,0,1;0rad)
  Placement2 = pos=(3e-16,4.8,12.75) rot=(-0.57735,-0.57735,-0.57735;2.0944rad)
  Reference1 = -> Assembly [magnet001.Face3,magnet001.Face3]
  Reference2 = -> Assembly [rotor.Face14,rotor.Face14]
  Suppressed = false
FEATURE [Assembly::JointGroup] Joints
  Group = -> [GroundedJoint,Joint,Joint001,Joint003,Joint007,Joint008,Joint009,Joint010,Joint011,Joint012,Joint013]
FEATURE [Assembly::AssemblyObject] Assembly
  Group = -> [Joints,rotor,bearing_body,GroundedJoint,bearing_holder,Joint,Joint001,coil_frame,Joint003,coil,coil001,Joint007,fused_crown,Exploded_Views,Exploded_View,Move004,Move005,Move,Move006,Move007,Move008,Move009,Move010,Joint008,Joint009,magnet,magnet001,magnet002,magnet003,Joint010,Joint011,Joint012,Joint013]
  Origin = -> Origin007
  Type = Assembly
FEATURE [Part::MultiCommon] Common  label="crown"
  Refine = true
  Shapes = -> [Fusion,Extrude]
FEATURE [App::Part] Part001  label="crown2"
  Group = -> [PolarArray,Sketch074,Sketch_On_Surface002,Mapped_Sketch002,Fusion,Extrude,Loft,Binder018,Mapped_Sketch003,Sketch_On_Surface003,Populate,Sketch073,Binder017,Common]
  Origin = -> Origin027
